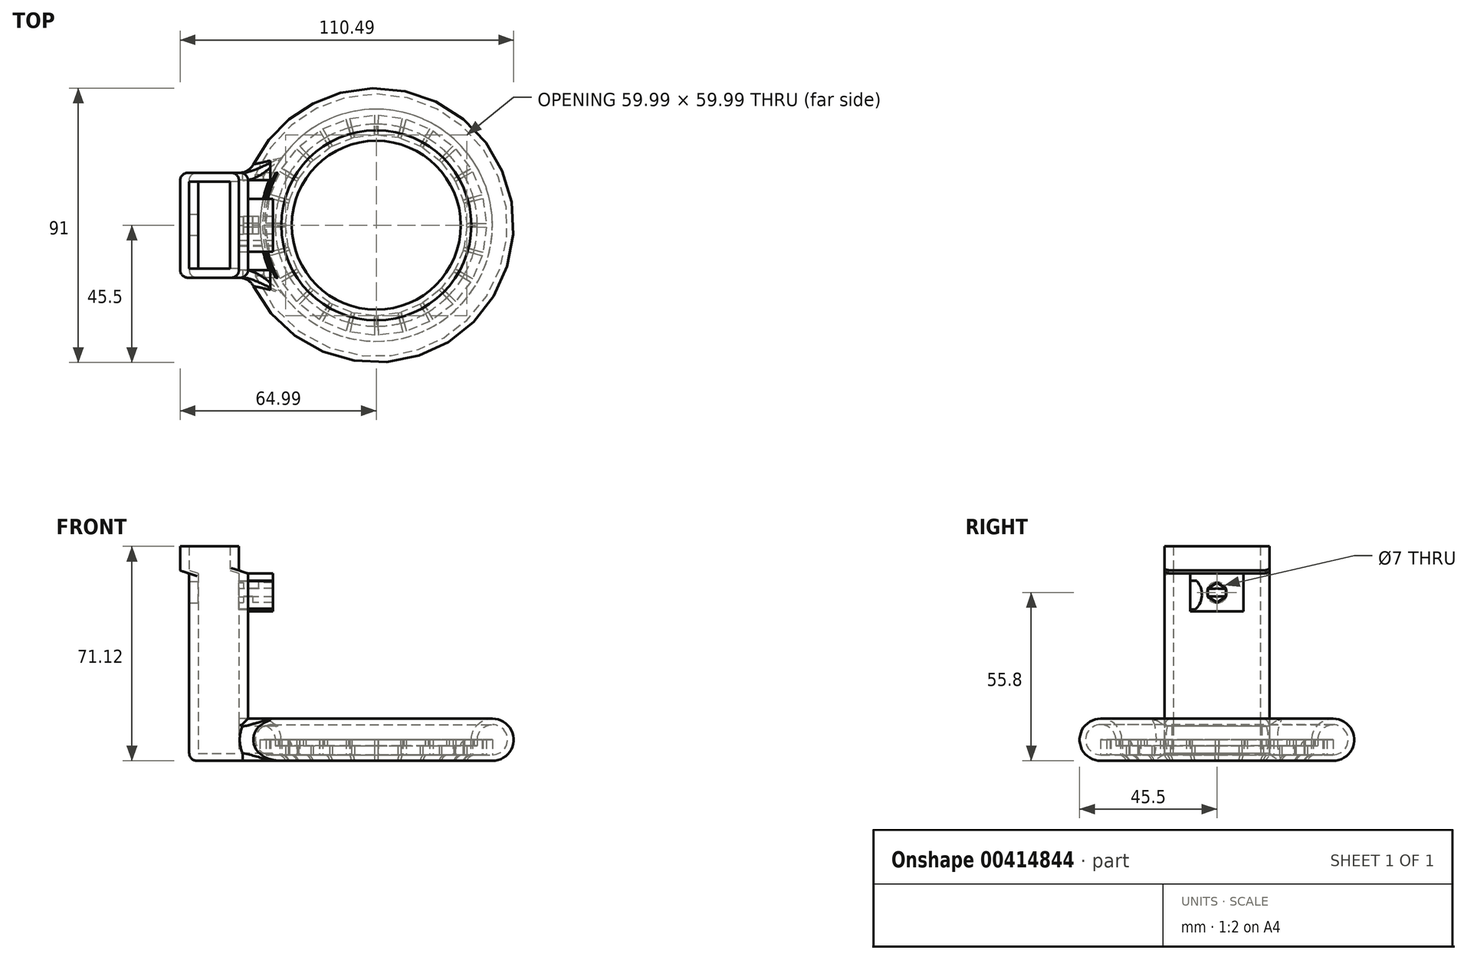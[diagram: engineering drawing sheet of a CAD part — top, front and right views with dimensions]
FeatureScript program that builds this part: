
annotation { "Feature Type Name" : "Feature", "Feature Type Description" : "" }
export const myFeature = defineFeature(function(context is Context, id is Id, definition is map)
    precondition{}
    {
        {
            var Q0;
            Q0=qCreatedBy(makeId("Right.planeOp"),FACE);
            cPlane(context, id + "F0", {"entities" : qUnion([Q0]), "cplaneType" : CPlaneType.OFFSET, "offset" : 42.5 * mm, "oppositeDirection" : true, "width" : 150 * mm, "height" : 150 * mm});
        }
        {
            var Q0;
            Q0=qCreatedBy(makeId("Front.planeOp"),FACE);
            cPlane(context, id + "F1", {"entities" : qUnion([Q0]), "cplaneType" : CPlaneType.OFFSET, "offset" : 17.41 * mm, "width" : 150 * mm, "height" : 150 * mm});
        }
        {
            var Q0;
            Q0=qCreatedBy(makeId("Front.planeOp"),FACE);
            cPlane(context, id + "F2", {"entities" : qUnion([Q0]), "cplaneType" : CPlaneType.OFFSET, "offset" : 17.41 * mm, "oppositeDirection" : true, "width" : 150 * mm, "height" : 150 * mm});
        }
        {
            var Q0;
            Q0=qCreatedBy(makeId("Top.planeOp"),FACE);
            cPlane(context, id + "F3", {"entities" : qUnion([Q0]), "cplaneType" : CPlaneType.OFFSET, "offset" : 7 * mm, "width" : 150 * mm, "height" : 150 * mm});
        }
        {
            var Q0;
            Q0=qCreatedBy(id+"F3.planeOp",FACE);
            cPlane(context, id + "F4", {"entities" : qUnion([Q0]), "cplaneType" : CPlaneType.OFFSET, "offset" : 6.95 * mm, "width" : 150 * mm, "height" : 150 * mm});
        }
        {
            var Q0;
            Q0=qCreatedBy(id+"F3.planeOp",FACE);
            cPlane(context, id + "F5", {"entities" : qUnion([Q0]), "cplaneType" : CPlaneType.OFFSET, "offset" : 55.12 * mm, "width" : 150 * mm, "height" : 150 * mm});
        }
        {
            var Q0;
            Q0=qCreatedBy(makeId("Right.planeOp"),FACE);
            cPlane(context, id + "F6", {"entities" : qUnion([Q0]), "cplaneType" : CPlaneType.OFFSET, "offset" : 62 * mm, "oppositeDirection" : true, "width" : 150 * mm, "height" : 150 * mm});
        }
        {
            var Q0;
            Q0=qCreatedBy(id+"F5.planeOp",FACE);
            cPlane(context, id + "F7", {"entities" : qUnion([Q0]), "cplaneType" : CPlaneType.OFFSET, "offset" : 1 * mm, "width" : 150 * mm, "height" : 150 * mm});
        }
        {
            var Q0;
            Q0=qCreatedBy(makeId("Top.planeOp"),FACE);
            var sketch = newSketch(context, id + "F8", { "sketchPlane" : qUnion([Q0])});
            skCircle(sketch, "E0", {"center": v(0, 0) * mm, "radius": 45 * mm});
            skCircle(sketch, "E1.0", {"center": v(0, 0) * mm, "radius": 38.5 * mm});
            skLineSegment(sketch, "E2", {"start": v(-136.41, 41.5) * mm, "end": v(-136.41, 35) * mm});
            skLineSegment(sketch, "E3", {"start": v(-128.72, 34) * mm, "end": v(-127.05, 40.28) * mm});
            skLineSegment(sketch, "E4", {"start": v(-118.16, 36.6) * mm, "end": v(-121.4, 30.99) * mm});
            skLineSegment(sketch, "E5", {"start": v(-115.15, 26.17) * mm, "end": v(-110.55, 30.76) * mm});
            skLineSegment(sketch, "E6", {"start": v(-110.44, 20.01) * mm, "end": v(-104.8, 23.26) * mm});
            skLineSegment(sketch, "E7", {"start": v(-107.45, 12.84) * mm, "end": v(-101.18, 14.54) * mm});
            skLineSegment(sketch, "E8", {"start": v(-106.41, 5.01) * mm, "end": v(-99.91, 5.01) * mm});
            skLineSegment(sketch, "E9.MirrorCS", {"start": v(-107.44, -2.81) * mm, "end": v(-101.17, -4.5) * mm});
            skLineSegment(sketch, "E10.MirrorCS", {"start": v(-110.42, -9.99) * mm, "end": v(-104.8, -13.24) * mm});
            skLineSegment(sketch, "E11.MirrorCS", {"start": v(-115.13, -16.15) * mm, "end": v(-110.52, -20.73) * mm});
            skLineSegment(sketch, "E12.MirrorCS", {"start": v(-118.13, -26.6) * mm, "end": v(-121.38, -20.97) * mm});
            skLineSegment(sketch, "E13.MirrorCS", {"start": v(-128.7, -24) * mm, "end": v(-127.02, -30.27) * mm});
            skLineSegment(sketch, "E14.MirrorCS", {"start": v(-144.1, 34) * mm, "end": v(-145.77, 40.28) * mm});
            skLineSegment(sketch, "E15.MirrorCS", {"start": v(-154.66, 36.6) * mm, "end": v(-151.41, 30.99) * mm});
            skLineSegment(sketch, "E16.MirrorCS", {"start": v(-157.67, 26.17) * mm, "end": v(-162.27, 30.76) * mm});
            skLineSegment(sketch, "E17.MirrorCS", {"start": v(-162.38, 20.01) * mm, "end": v(-168.01, 23.26) * mm});
            skLineSegment(sketch, "E18.MirrorCS", {"start": v(-165.37, 12.84) * mm, "end": v(-171.64, 14.54) * mm});
            skLineSegment(sketch, "E19.MirrorCS", {"start": v(-165.38, -2.81) * mm, "end": v(-171.65, -4.5) * mm});
            skLineSegment(sketch, "E20.MirrorCS", {"start": v(-162.4, -9.99) * mm, "end": v(-168.03, -13.24) * mm});
            skLineSegment(sketch, "E21.MirrorCS", {"start": v(-157.69, -16.15) * mm, "end": v(-162.3, -20.73) * mm});
            skLineSegment(sketch, "E22.MirrorCS", {"start": v(-154.69, -26.6) * mm, "end": v(-151.44, -20.97) * mm});
            skLineSegment(sketch, "E23.MirrorCS", {"start": v(-144.13, -24) * mm, "end": v(-145.8, -30.27) * mm});
            skLineSegment(sketch, "E24", {"start": v(-136.41, -25) * mm, "end": v(-136.41, -31.5) * mm});
            skLineSegment(sketch, "E25", {"start": v(-166.41, 5) * mm, "end": v(-172.91, 5) * mm});
            skCircle(sketch, "E26", {"center": v(-136.41, 5) * mm, "radius": 1.25 * mm, "construction": true});
            skLineSegment(sketch, "E27", {"start": v(0.64, 36.5) * mm, "end": v(0.52, 30) * mm});
            skLineSegment(sketch, "E28", {"start": v(8.2, 28.86) * mm, "end": v(9.97, 35.11) * mm});
            skLineSegment(sketch, "E29", {"start": v(18.8, 31.29) * mm, "end": v(15.46, 25.72) * mm});
            skLineSegment(sketch, "E30", {"start": v(21.62, 20.8) * mm, "end": v(26.3, 25.3) * mm});
            skLineSegment(sketch, "E31", {"start": v(26.23, 14.56) * mm, "end": v(31.92, 17.71) * mm});
            skLineSegment(sketch, "E32", {"start": v(29.1, 7.33) * mm, "end": v(35.4, 8.92) * mm});
            skLineSegment(sketch, "E33", {"start": v(30, -0.5) * mm, "end": v(36.5, -0.62) * mm});
            skLineSegment(sketch, "E34.MirrorCS", {"start": v(28.82, -8.32) * mm, "end": v(35.07, -10.12) * mm});
            skLineSegment(sketch, "E35.MirrorCS", {"start": v(25.72, -15.44) * mm, "end": v(31.3, -18.78) * mm});
            skLineSegment(sketch, "E36.MirrorCS", {"start": v(20.9, -21.52) * mm, "end": v(25.43, -26.18) * mm});
            skLineSegment(sketch, "E37.MirrorCS", {"start": v(17.73, -31.9) * mm, "end": v(14.57, -26.23) * mm});
            skLineSegment(sketch, "E38.MirrorCS", {"start": v(7.21, -29.12) * mm, "end": v(8.77, -35.43) * mm});
            skLineSegment(sketch, "E39.MirrorCS", {"start": v(-7.18, 29.13) * mm, "end": v(-8.74, 35.44) * mm});
            skLineSegment(sketch, "E40.MirrorCS", {"start": v(-17.7, 31.92) * mm, "end": v(-14.55, 26.25) * mm});
            skLineSegment(sketch, "E41.MirrorCS", {"start": v(-20.88, 21.54) * mm, "end": v(-25.4, 26.2) * mm});
            skLineSegment(sketch, "E42.MirrorCS", {"start": v(-25.7, 15.46) * mm, "end": v(-31.28, 18.81) * mm});
            skLineSegment(sketch, "E43.MirrorCS", {"start": v(-28.82, 8.34) * mm, "end": v(-35.06, 10.15) * mm});
            skLineSegment(sketch, "E44.MirrorCS", {"start": v(-29.1, -7.3) * mm, "end": v(-35.4, -8.89) * mm});
            skLineSegment(sketch, "E45.MirrorCS", {"start": v(-26.25, -14.53) * mm, "end": v(-31.93, -17.68) * mm});
            skLineSegment(sketch, "E46.MirrorCS", {"start": v(-21.64, -20.77) * mm, "end": v(-26.33, -25.28) * mm});
            skLineSegment(sketch, "E47.MirrorCS", {"start": v(-18.83, -31.27) * mm, "end": v(-15.48, -25.7) * mm});
            skLineSegment(sketch, "E48.MirrorCS", {"start": v(-8.22, -28.85) * mm, "end": v(-10, -35.1) * mm});
            skLineSegment(sketch, "E49", {"start": v(-0.52, -30) * mm, "end": v(-0.64, -36.5) * mm});
            skLineSegment(sketch, "E50", {"start": v(-30, 0.52) * mm, "end": v(-36.5, 0.64) * mm});
            skLineSegment(sketch, "E51", {"start": v(-0.64, 36.5) * mm, "end": v(-0.52, 30) * mm});
            skLineSegment(sketch, "E52", {"start": v(7.18, 29.13) * mm, "end": v(8.74, 35.44) * mm});
            skLineSegment(sketch, "E53", {"start": v(17.7, 31.92) * mm, "end": v(14.55, 26.25) * mm});
            skLineSegment(sketch, "E54", {"start": v(20.88, 21.54) * mm, "end": v(25.4, 26.2) * mm});
            skLineSegment(sketch, "E55", {"start": v(25.7, 15.46) * mm, "end": v(31.28, 18.81) * mm});
            skLineSegment(sketch, "E56", {"start": v(28.82, 8.34) * mm, "end": v(35.06, 10.15) * mm});
            skLineSegment(sketch, "E57", {"start": v(30, 0.54) * mm, "end": v(36.5, 0.65) * mm});
            skLineSegment(sketch, "E58.MirrorCS", {"start": v(29.1, -7.3) * mm, "end": v(35.4, -8.89) * mm});
            skLineSegment(sketch, "E59.MirrorCS", {"start": v(26.25, -14.53) * mm, "end": v(31.93, -17.68) * mm});
            skLineSegment(sketch, "E60.MirrorCS", {"start": v(21.64, -20.77) * mm, "end": v(26.33, -25.28) * mm});
            skLineSegment(sketch, "E61.MirrorCS", {"start": v(18.83, -31.27) * mm, "end": v(15.48, -25.7) * mm});
            skLineSegment(sketch, "E62.MirrorCS", {"start": v(8.22, -28.85) * mm, "end": v(10, -35.1) * mm});
            skLineSegment(sketch, "E63.MirrorCS", {"start": v(-8.2, 28.86) * mm, "end": v(-9.97, 35.11) * mm});
            skLineSegment(sketch, "E64.MirrorCS", {"start": v(-18.8, 31.29) * mm, "end": v(-15.46, 25.72) * mm});
            skLineSegment(sketch, "E65.MirrorCS", {"start": v(-21.62, 20.8) * mm, "end": v(-26.3, 25.3) * mm});
            skLineSegment(sketch, "E66.MirrorCS", {"start": v(-26.23, 14.56) * mm, "end": v(-31.92, 17.71) * mm});
            skLineSegment(sketch, "E67.MirrorCS", {"start": v(-29.1, 7.33) * mm, "end": v(-35.4, 8.92) * mm});
            skLineSegment(sketch, "E68.MirrorCS", {"start": v(-28.82, -8.32) * mm, "end": v(-35.07, -10.12) * mm});
            skLineSegment(sketch, "E69.MirrorCS", {"start": v(-25.72, -15.44) * mm, "end": v(-31.3, -18.78) * mm});
            skLineSegment(sketch, "E70.MirrorCS", {"start": v(-20.9, -21.52) * mm, "end": v(-25.43, -26.18) * mm});
            skLineSegment(sketch, "E71.MirrorCS", {"start": v(-17.73, -31.9) * mm, "end": v(-14.57, -26.23) * mm});
            skLineSegment(sketch, "E72.MirrorCS", {"start": v(-7.21, -29.12) * mm, "end": v(-8.77, -35.43) * mm});
            skLineSegment(sketch, "E73", {"start": v(0.52, -30) * mm, "end": v(0.64, -36.5) * mm});
            skLineSegment(sketch, "E74", {"start": v(-30, -0.52) * mm, "end": v(-36.5, -0.64) * mm});
            skCircle(sketch, "E75", {"center": v(0, 0) * mm, "radius": 1.25 * mm, "construction": true});
            skLineSegment(sketch, "E76", {"start": v(-29.1, 7.33) * mm, "end": v(-28.82, 8.34) * mm});
            skLineSegment(sketch, "E77", {"start": v(-28.82, 8.34) * mm, "end": v(-26.23, 14.56) * mm});
            skLineSegment(sketch, "E78", {"start": v(-26.23, 14.56) * mm, "end": v(-25.7, 15.46) * mm});
            skLineSegment(sketch, "E79", {"start": v(-25.7, 15.46) * mm, "end": v(-21.62, 20.8) * mm});
            skLineSegment(sketch, "E80", {"start": v(-21.62, 20.8) * mm, "end": v(-20.88, 21.54) * mm});
            skLineSegment(sketch, "E81", {"start": v(-20.88, 21.54) * mm, "end": v(-15.46, 25.72) * mm});
            skLineSegment(sketch, "E82", {"start": v(-15.46, 25.72) * mm, "end": v(-14.55, 26.25) * mm});
            skLineSegment(sketch, "E83", {"start": v(-14.55, 26.25) * mm, "end": v(-8.2, 28.86) * mm});
            skLineSegment(sketch, "E84", {"start": v(-8.2, 28.86) * mm, "end": v(-7.18, 29.13) * mm});
            skLineSegment(sketch, "E85", {"start": v(-7.18, 29.13) * mm, "end": v(-0.52, 30) * mm});
            skLineSegment(sketch, "E86", {"start": v(-0.52, 30) * mm, "end": v(0.52, 30) * mm});
            skLineSegment(sketch, "E87", {"start": v(0.52, 30) * mm, "end": v(7.18, 29.13) * mm});
            skLineSegment(sketch, "E88", {"start": v(7.18, 29.13) * mm, "end": v(8.2, 28.86) * mm});
            skLineSegment(sketch, "E89", {"start": v(8.2, 28.86) * mm, "end": v(14.55, 26.25) * mm});
            skLineSegment(sketch, "E90", {"start": v(14.55, 26.25) * mm, "end": v(15.46, 25.72) * mm});
            skLineSegment(sketch, "E91", {"start": v(15.46, 25.72) * mm, "end": v(20.88, 21.54) * mm});
            skLineSegment(sketch, "E92", {"start": v(20.88, 21.54) * mm, "end": v(21.62, 20.8) * mm});
            skLineSegment(sketch, "E93", {"start": v(21.62, 20.8) * mm, "end": v(25.7, 15.46) * mm});
            skLineSegment(sketch, "E94", {"start": v(25.7, 15.46) * mm, "end": v(26.23, 14.56) * mm});
            skLineSegment(sketch, "E95", {"start": v(26.23, 14.56) * mm, "end": v(28.82, 8.34) * mm});
            skLineSegment(sketch, "E96", {"start": v(28.82, 8.34) * mm, "end": v(29.1, 7.33) * mm});
            skLineSegment(sketch, "E97", {"start": v(29.1, 7.33) * mm, "end": v(30, 0.54) * mm});
            skLineSegment(sketch, "E98", {"start": v(30, 0.54) * mm, "end": v(30, -0.5) * mm});
            skLineSegment(sketch, "E99", {"start": v(30, -0.5) * mm, "end": v(29.1, -7.3) * mm});
            skLineSegment(sketch, "E100", {"start": v(29.1, -7.3) * mm, "end": v(28.82, -8.32) * mm});
            skLineSegment(sketch, "E101", {"start": v(28.82, -8.32) * mm, "end": v(26.25, -14.53) * mm});
            skLineSegment(sketch, "E102", {"start": v(26.25, -14.53) * mm, "end": v(25.72, -15.44) * mm});
            skLineSegment(sketch, "E103", {"start": v(25.72, -15.44) * mm, "end": v(21.64, -20.77) * mm});
            skLineSegment(sketch, "E104", {"start": v(21.64, -20.77) * mm, "end": v(20.9, -21.52) * mm});
            skLineSegment(sketch, "E105", {"start": v(20.9, -21.52) * mm, "end": v(15.48, -25.7) * mm});
            skLineSegment(sketch, "E106", {"start": v(15.48, -25.7) * mm, "end": v(14.57, -26.23) * mm});
            skLineSegment(sketch, "E107", {"start": v(14.57, -26.23) * mm, "end": v(8.22, -28.85) * mm});
            skLineSegment(sketch, "E108", {"start": v(8.22, -28.85) * mm, "end": v(7.21, -29.12) * mm});
            skLineSegment(sketch, "E109", {"start": v(7.21, -29.12) * mm, "end": v(0.52, -30) * mm});
            skLineSegment(sketch, "E110", {"start": v(0.52, -30) * mm, "end": v(-0.52, -30) * mm});
            skLineSegment(sketch, "E111", {"start": v(-0.52, -30) * mm, "end": v(-7.21, -29.12) * mm});
            skLineSegment(sketch, "E112", {"start": v(-7.21, -29.12) * mm, "end": v(-8.22, -28.85) * mm});
            skLineSegment(sketch, "E113", {"start": v(-8.22, -28.85) * mm, "end": v(-14.57, -26.23) * mm});
            skLineSegment(sketch, "E114", {"start": v(-14.57, -26.23) * mm, "end": v(-15.48, -25.7) * mm});
            skLineSegment(sketch, "E115", {"start": v(-15.48, -25.7) * mm, "end": v(-20.9, -21.52) * mm});
            skLineSegment(sketch, "E116", {"start": v(-20.9, -21.52) * mm, "end": v(-21.64, -20.77) * mm});
            skLineSegment(sketch, "E117", {"start": v(-21.64, -20.77) * mm, "end": v(-25.72, -15.44) * mm});
            skLineSegment(sketch, "E118", {"start": v(-25.72, -15.44) * mm, "end": v(-26.25, -14.53) * mm});
            skLineSegment(sketch, "E119", {"start": v(-28.82, -8.32) * mm, "end": v(-29.1, -7.3) * mm});
            skLineSegment(sketch, "E120", {"start": v(-26.25, -14.53) * mm, "end": v(-28.82, -8.32) * mm});
            skLineSegment(sketch, "E121", {"start": v(-29.1, -7.3) * mm, "end": v(-30, -0.52) * mm});
            skLineSegment(sketch, "E122", {"start": v(-30, -0.52) * mm, "end": v(-30, 0.52) * mm});
            skLineSegment(sketch, "E123", {"start": v(-30, 0.52) * mm, "end": v(-29.1, 7.33) * mm});
            skLineSegment(sketch, "E124", {"start": v(-36.5, 0.64) * mm, "end": v(-35.4, 8.92) * mm});
            skLineSegment(sketch, "E125", {"start": v(-35.06, 10.15) * mm, "end": v(-31.92, 17.71) * mm});
            skLineSegment(sketch, "E126", {"start": v(-31.28, 18.81) * mm, "end": v(-26.3, 25.3) * mm});
            skLineSegment(sketch, "E127", {"start": v(-25.4, 26.2) * mm, "end": v(-18.8, 31.29) * mm});
            skLineSegment(sketch, "E128", {"start": v(-17.7, 31.92) * mm, "end": v(-9.97, 35.11) * mm});
            skLineSegment(sketch, "E129", {"start": v(-8.74, 35.44) * mm, "end": v(-0.64, 36.5) * mm});
            skLineSegment(sketch, "E130", {"start": v(0.64, 36.5) * mm, "end": v(8.74, 35.44) * mm});
            skLineSegment(sketch, "E131", {"start": v(9.97, 35.11) * mm, "end": v(17.7, 31.92) * mm});
            skLineSegment(sketch, "E132", {"start": v(18.8, 31.29) * mm, "end": v(25.4, 26.2) * mm});
            skLineSegment(sketch, "E133", {"start": v(26.3, 25.3) * mm, "end": v(31.28, 18.81) * mm});
            skLineSegment(sketch, "E134", {"start": v(31.92, 17.71) * mm, "end": v(35.06, 10.15) * mm});
            skLineSegment(sketch, "E135", {"start": v(35.4, 8.92) * mm, "end": v(36.5, 0.65) * mm});
            skLineSegment(sketch, "E136", {"start": v(36.5, -0.62) * mm, "end": v(35.4, -8.89) * mm});
            skLineSegment(sketch, "E137", {"start": v(35.07, -10.12) * mm, "end": v(31.93, -17.68) * mm});
            skLineSegment(sketch, "E138", {"start": v(31.3, -18.78) * mm, "end": v(26.33, -25.28) * mm});
            skLineSegment(sketch, "E139", {"start": v(25.43, -26.18) * mm, "end": v(18.83, -31.27) * mm});
            skLineSegment(sketch, "E140", {"start": v(17.73, -31.9) * mm, "end": v(10, -35.1) * mm});
            skLineSegment(sketch, "E141", {"start": v(8.77, -35.43) * mm, "end": v(0.64, -36.5) * mm});
            skLineSegment(sketch, "E142", {"start": v(-0.64, -36.5) * mm, "end": v(-8.77, -35.43) * mm});
            skLineSegment(sketch, "E143", {"start": v(-10, -35.1) * mm, "end": v(-17.73, -31.9) * mm});
            skLineSegment(sketch, "E144", {"start": v(-18.83, -31.27) * mm, "end": v(-25.43, -26.18) * mm});
            skLineSegment(sketch, "E145", {"start": v(-26.33, -25.28) * mm, "end": v(-31.3, -18.78) * mm});
            skLineSegment(sketch, "E146", {"start": v(-31.93, -17.68) * mm, "end": v(-35.07, -10.12) * mm});
            skLineSegment(sketch, "E147", {"start": v(-35.4, -8.89) * mm, "end": v(-36.5, -0.64) * mm});
            skSolve(sketch);
        }
        {
            var Q0;
            Q0=qCreatedBy(makeId("Front.planeOp"),FACE);
            var sketch = newSketch(context, id + "F9", { "sketchPlane" : qUnion([Q0])});
            skLineSegment(sketch, "E148.bottom", {"start": v(38.5, 7) * mm, "end": v(-38.5, 7) * mm, "construction": true});
            skLineSegment(sketch, "E148.top", {"start": v(38.5, -7) * mm, "end": v(-38.5, -7) * mm, "construction": true});
            skLineSegment(sketch, "E148.left", {"start": v(38.5, 7) * mm, "end": v(38.5, -7) * mm, "construction": true});
            skLineSegment(sketch, "E148.right", {"start": v(-38.5, 7) * mm, "end": v(-38.5, -7) * mm, "construction": true});
            skPoint(sketch, "E148.middle", {"position": v(0, 0) * mm});
            skLineSegment(sketch, "E149", {"start": v(-38.5, 0) * mm, "end": v(38.5, 0) * mm, "construction": true});
            skArc(sketch, "E150", {"start": v(38.5, 0) * mm, "mid": v(43.45, 11.95) * mm, "end": v(31.5, 7) * mm});
            skArc(sketch, "E151", {"start": v(38.5, 2) * mm, "mid": v(42.04, 10.54) * mm, "end": v(33.5, 7) * mm});
            skLineSegment(sketch, "E152", {"start": v(38.5, 2) * mm, "end": v(38.5, 0) * mm});
            skLineSegment(sketch, "E153", {"start": v(38.5, 2) * mm, "end": v(31.5, 2) * mm, "construction": true});
            skLineSegment(sketch, "E154", {"start": v(31.5, 2) * mm, "end": v(31.5, 0) * mm, "construction": true});
            skLineSegment(sketch, "E155.0", {"start": v(38.5, 5) * mm, "end": v(-38.5, 5) * mm, "construction": true});
            skLineSegment(sketch, "E156", {"start": v(30, 0) * mm, "end": v(30, 7) * mm, "construction": true});
            skLineSegment(sketch, "E157", {"start": v(31.5, 7) * mm, "end": v(30, 7) * mm});
            skLineSegment(sketch, "E158", {"start": v(30, 7) * mm, "end": v(30, 5) * mm});
            skLineSegment(sketch, "E159", {"start": v(30, 5) * mm, "end": v(33.5, 5) * mm});
            skLineSegment(sketch, "E160", {"start": v(33.5, 5) * mm, "end": v(33.5, 7) * mm});
            skLineSegment(sketch, "E161", {"start": v(0, -7) * mm, "end": v(0, 7) * mm, "construction": true});
            skLineSegment(sketch, "E162", {"start": v(38.5, 7) * mm, "end": v(38.5, 14) * mm, "construction": true});
            skLineSegment(sketch, "E163", {"start": v(38.5, 7) * mm, "end": v(45.5, 7) * mm, "construction": true});
            skLineSegment(sketch, "E164", {"start": v(38.5, 12) * mm, "end": v(38.5, 14) * mm});
            skLineSegment(sketch, "E165", {"start": v(43.5, 7) * mm, "end": v(45.5, 7) * mm});
            skLineSegment(sketch, "E166.MirrorCS", {"start": v(-38.5, 2) * mm, "end": v(-38.5, 0) * mm});
            skLineSegment(sketch, "E167.MirrorCS", {"start": v(-30, 7) * mm, "end": v(-30, 5) * mm});
            skLineSegment(sketch, "E168.MirrorCS", {"start": v(-31.5, 7) * mm, "end": v(-30, 7) * mm});
            skLineSegment(sketch, "E169.MirrorCS", {"start": v(-33.5, 5) * mm, "end": v(-33.5, 7) * mm});
            skLineSegment(sketch, "E170.MirrorCS", {"start": v(-43.5, 7) * mm, "end": v(-45.5, 7) * mm});
            skLineSegment(sketch, "E171.MirrorCS", {"start": v(-30, 5) * mm, "end": v(-33.5, 5) * mm});
            skLineSegment(sketch, "E172.MirrorCS", {"start": v(-31.5, 2) * mm, "end": v(-31.5, 0) * mm, "construction": true});
            skLineSegment(sketch, "E173.MirrorCS", {"start": v(-38.5, 12) * mm, "end": v(-38.5, 14) * mm});
            skLineSegment(sketch, "E174.MirrorCS", {"start": v(-38.5, 7) * mm, "end": v(-45.5, 7) * mm, "construction": true});
            skLineSegment(sketch, "E175.MirrorCS", {"start": v(-38.5, 2) * mm, "end": v(-31.5, 2) * mm, "construction": true});
            skLineSegment(sketch, "E176.MirrorCS", {"start": v(-38.5, 7) * mm, "end": v(-38.5, 14) * mm, "construction": true});
            skArc(sketch, "E177.MirrorCS", {"start": v(-38.5, 0) * mm, "mid": v(-43.45, 11.95) * mm, "end": v(-31.5, 7) * mm});
            skArc(sketch, "E178.MirrorCS", {"start": v(-38.5, 2) * mm, "mid": v(-42.04, 10.54) * mm, "end": v(-33.5, 7) * mm});
            skLineSegment(sketch, "E179.MirrorCS", {"start": v(-38.5, 5) * mm, "end": v(38.5, 5) * mm, "construction": true});
            skLineSegment(sketch, "E180.MirrorCS", {"start": v(-30, 0) * mm, "end": v(-30, 7) * mm, "construction": true});
            skLineSegment(sketch, "E181.MirrorCS", {"start": v(-38.5, 7) * mm, "end": v(38.5, 7) * mm, "construction": true});
            skArc(sketch, "E182", {"start": v(30, 7) * mm, "mid": v(28.58, 6.41) * mm, "end": v(28, 5) * mm});
            skLineSegment(sketch, "E183", {"start": v(28, 5) * mm, "end": v(30, 5) * mm});
            skArc(sketch, "E184.MirrorCS", {"start": v(-30, 7) * mm, "mid": v(-28.58, 6.41) * mm, "end": v(-28, 5) * mm});
            skLineSegment(sketch, "E185", {"start": v(-30, 5) * mm, "end": v(-28, 5) * mm});
            skSolve(sketch);
        }
        {
            var Q0;
            Q0=qCreatedBy(id+"F0.planeOp",FACE);
            var sketch = newSketch(context, id + "F10", { "sketchPlane" : qUnion([Q0])});
            skLineSegment(sketch, "E186.bottom", {"start": v(45.5, 14) * mm, "end": v(-45.5, 14) * mm, "construction": true});
            skLineSegment(sketch, "E186.top", {"start": v(45.5, -14) * mm, "end": v(-45.5, -14) * mm, "construction": true});
            skLineSegment(sketch, "E186.left", {"start": v(45.5, 14) * mm, "end": v(45.5, -14) * mm, "construction": true});
            skLineSegment(sketch, "E186.right", {"start": v(-45.5, 14) * mm, "end": v(-45.5, -14) * mm, "construction": true});
            skPoint(sketch, "E186.middle", {"position": v(0, 0) * mm});
            skLineSegment(sketch, "E187", {"start": v(-45.5, 0) * mm, "end": v(45.5, 0) * mm, "construction": true});
            skLineSegment(sketch, "E188", {"start": v(0, 14) * mm, "end": v(0, -14) * mm, "construction": true});
            skLineSegment(sketch, "E189.0", {"start": v(-17.41, 14) * mm, "end": v(-17.41, -14) * mm, "construction": true});
            skLineSegment(sketch, "E190.MirrorCS", {"start": v(17.41, 14) * mm, "end": v(17.41, -14) * mm, "construction": true});
            skLineSegment(sketch, "E191.0", {"start": v(45.5, 7) * mm, "end": v(-45.5, 7) * mm, "construction": true});
            skLineSegment(sketch, "E192", {"start": v(-17.41, 14) * mm, "end": v(-17.41, 7) * mm});
            skLineSegment(sketch, "E193", {"start": v(-17.41, 7) * mm, "end": v(17.41, 7) * mm});
            skLineSegment(sketch, "E194", {"start": v(17.41, 7) * mm, "end": v(17.41, 14) * mm});
            skLineSegment(sketch, "E195", {"start": v(17.41, 14) * mm, "end": v(-17.41, 14) * mm});
            skLineSegment(sketch, "E196.0", {"start": v(45.5, 12) * mm, "end": v(-45.5, 12) * mm, "construction": true});
            skLineSegment(sketch, "E197.0", {"start": v(-14.73, 14) * mm, "end": v(-14.73, -14) * mm, "construction": true});
            skLineSegment(sketch, "E198.MirrorCS", {"start": v(14.73, 14) * mm, "end": v(14.73, -14) * mm, "construction": true});
            skLineSegment(sketch, "E199", {"start": v(-14.73, 7) * mm, "end": v(-14.73, 14) * mm});
            skLineSegment(sketch, "E200", {"start": v(14.73, 7) * mm, "end": v(14.73, 14) * mm});
            skLineSegment(sketch, "E201", {"start": v(17.41, 12) * mm, "end": v(-17.41, 12) * mm});
            skPoint(sketch, "E201.startSnap0", {"position": v(17.41, 10.5) * mm});
            skArc(sketch, "E202.0", {"start": v(6.63, 59.56) * mm, "mid": v(4.95, 54.97) * mm, "end": v(6.87, 50.47) * mm});
            skArc(sketch, "E203.MirrorCS", {"start": v(-6.63, 59.56) * mm, "mid": v(-4.95, 54.97) * mm, "end": v(-6.87, 50.47) * mm});
            skLineSegment(sketch, "E204", {"start": v(-6.63, 59.72) * mm, "end": v(6.63, 59.72) * mm});
            skLineSegment(sketch, "E205.1", {"start": v(-2.98, 51.95) * mm, "end": v(2.98, 51.95) * mm});
            skLineSegment(sketch, "E206", {"start": v(-8.8, 49.55) * mm, "end": v(-8.8, 62.12) * mm});
            skLineSegment(sketch, "E207.MirrorCS", {"start": v(8.8, 49.55) * mm, "end": v(8.8, 62.12) * mm});
            skLineSegment(sketch, "E208", {"start": v(-8.8, 62.12) * mm, "end": v(8.8, 62.12) * mm});
            skLineSegment(sketch, "E209", {"start": v(-6.63, 59.72) * mm, "end": v(-8.8, 59.72) * mm});
            skLineSegment(sketch, "E210", {"start": v(6.63, 59.72) * mm, "end": v(8.8, 59.72) * mm});
            skLineSegment(sketch, "E211", {"start": v(-2.98, 51.95) * mm, "end": v(-6.87, 50.26) * mm});
            skLineSegment(sketch, "E212", {"start": v(-6.87, 50.47) * mm, "end": v(-6.87, 50.26) * mm});
            skLineSegment(sketch, "E213.MirrorCS", {"start": v(2.98, 51.95) * mm, "end": v(6.87, 50.26) * mm});
            skLineSegment(sketch, "E214.MirrorCS", {"start": v(6.87, 50.47) * mm, "end": v(6.87, 50.26) * mm});
            skLineSegment(sketch, "E215", {"start": v(-8.8, 49.55) * mm, "end": v(8.8, 49.55) * mm});
            skLineSegment(sketch, "E216", {"start": v(6.87, 50.26) * mm, "end": v(8.8, 50.26) * mm});
            skLineSegment(sketch, "E217", {"start": v(-6.87, 50.26) * mm, "end": v(-8.8, 50.26) * mm});
            skCircle(sketch, "E218", {"center": v(0, 0) * mm, "radius": 1.5 * mm, "construction": true});
            skCircle(sketch, "E219", {"center": v(0, 55.8) * mm, "radius": 1.39 * mm});
            skLineSegment(sketch, "E220", {"start": v(6.63, 59.56) * mm, "end": v(6.63, 59.72) * mm});
            skLineSegment(sketch, "E221", {"start": v(-6.63, 59.56) * mm, "end": v(-6.63, 59.72) * mm});
            skLineSegment(sketch, "E222.1", {"start": v(0, 52.5) * mm, "end": v(2.95, 54.35) * mm});
            skLineSegment(sketch, "E222.2", {"start": v(-2.95, 54.35) * mm, "end": v(0, 52.5) * mm});
            skLineSegment(sketch, "E223.MirrorCS", {"start": v(0, 59.1) * mm, "end": v(2.95, 57.25) * mm});
            skLineSegment(sketch, "E224.MirrorCS", {"start": v(-2.95, 57.25) * mm, "end": v(0, 59.1) * mm});
            skLineSegment(sketch, "E225", {"start": v(2.95, 57.25) * mm, "end": v(2.95, 54.35) * mm});
            skLineSegment(sketch, "E226", {"start": v(-2.95, 57.25) * mm, "end": v(-2.95, 54.35) * mm});
            skCircle(sketch, "E227", {"center": v(0, 55.8) * mm, "radius": 1.25 * mm, "construction": true});
            skLineSegment(sketch, "E228", {"start": v(-2.95, 54.55) * mm, "end": v(2.95, 54.55) * mm});
            skLineSegment(sketch, "E229", {"start": v(-2.95, 57.05) * mm, "end": v(2.95, 57.05) * mm});
            skLineSegment(sketch, "E230", {"start": v(14.73, 14) * mm, "end": v(14.73, 52.5) * mm});
            skLineSegment(sketch, "E231", {"start": v(0, 55.8) * mm, "end": v(0, 14) * mm, "construction": true});
            skLineSegment(sketch, "E232.MirrorCS", {"start": v(-14.73, 14) * mm, "end": v(-14.73, 52.5) * mm});
            skLineSegment(sketch, "E233", {"start": v(17.41, 14) * mm, "end": v(17.41, 52.5) * mm});
            skLineSegment(sketch, "E234", {"start": v(-17.41, 14) * mm, "end": v(-17.41, 52.5) * mm});
            skLineSegment(sketch, "E235", {"start": v(-8.8, 62.12) * mm, "end": v(-17.41, 62.12) * mm});
            skLineSegment(sketch, "E236", {"start": v(8.8, 62.12) * mm, "end": v(17.41, 62.12) * mm});
            skLineSegment(sketch, "E237", {"start": v(17.41, 52.5) * mm, "end": v(17.41, 62.12) * mm});
            skLineSegment(sketch, "E238", {"start": v(14.73, 52.5) * mm, "end": v(14.73, 62.12) * mm});
            skLineSegment(sketch, "E239", {"start": v(-14.73, 52.5) * mm, "end": v(-14.73, 62.12) * mm});
            skLineSegment(sketch, "E240", {"start": v(-17.41, 52.5) * mm, "end": v(-17.41, 62.12) * mm});
            skSolve(sketch);
        }
        {
            var Q0;
            Q0=qCreatedBy(id+"F1.planeOp",FACE);
            var sketch = newSketch(context, id + "F11", { "sketchPlane" : qUnion([Q0])});
            skLineSegment(sketch, "E241.bottom", {"start": v(45.5, 14) * mm, "end": v(-45.5, 14) * mm, "construction": true});
            skLineSegment(sketch, "E241.top", {"start": v(45.5, -14) * mm, "end": v(-45.5, -14) * mm, "construction": true});
            skLineSegment(sketch, "E241.left", {"start": v(45.5, 14) * mm, "end": v(45.5, -14) * mm, "construction": true});
            skLineSegment(sketch, "E241.right", {"start": v(-45.5, 14) * mm, "end": v(-45.5, -14) * mm, "construction": true});
            skPoint(sketch, "E241.middle", {"position": v(0, 0) * mm});
            skLineSegment(sketch, "E242", {"start": v(-45.5, 0) * mm, "end": v(45.5, 0) * mm, "construction": true});
            skLineSegment(sketch, "E243", {"start": v(0, 14) * mm, "end": v(0, -14) * mm, "construction": true});
            skLineSegment(sketch, "E244.0", {"start": v(-17.41, 14) * mm, "end": v(-17.41, -14) * mm, "construction": true});
            skLineSegment(sketch, "E245.MirrorCS", {"start": v(17.41, 14) * mm, "end": v(17.41, -14) * mm, "construction": true});
            skLineSegment(sketch, "E246.0", {"start": v(45.5, 7) * mm, "end": v(-45.5, 7) * mm, "construction": true});
            skLineSegment(sketch, "E247", {"start": v(-17.41, 14) * mm, "end": v(-17.41, 7) * mm});
            skLineSegment(sketch, "E248", {"start": v(-17.41, 7) * mm, "end": v(17.41, 7) * mm});
            skLineSegment(sketch, "E249", {"start": v(17.41, 7) * mm, "end": v(17.41, 14) * mm});
            skLineSegment(sketch, "E250", {"start": v(17.41, 14) * mm, "end": v(-17.41, 14) * mm});
            skLineSegment(sketch, "E251.0", {"start": v(45.5, 12) * mm, "end": v(-45.5, 12) * mm, "construction": true});
            skLineSegment(sketch, "E252.0", {"start": v(-14.73, 14) * mm, "end": v(-14.73, -14) * mm, "construction": true});
            skLineSegment(sketch, "E253.MirrorCS", {"start": v(14.73, 14) * mm, "end": v(14.73, -14) * mm, "construction": true});
            skLineSegment(sketch, "E254", {"start": v(-14.73, 7) * mm, "end": v(-14.73, 14) * mm});
            skLineSegment(sketch, "E255", {"start": v(14.73, 7) * mm, "end": v(14.73, 14) * mm});
            skLineSegment(sketch, "E256", {"start": v(17.41, 12) * mm, "end": v(-17.41, 12) * mm});
            skPoint(sketch, "E256.startSnap0", {"position": v(17.41, 10.5) * mm});
            skLineSegment(sketch, "E257", {"start": v(45.5, 14) * mm, "end": v(45.5, 7) * mm});
            skCircle(sketch, "E258", {"center": v(-35.07, 7) * mm, "radius": 7 * mm, "construction": true});
            skArc(sketch, "E259", {"start": v(-35.07, 12) * mm, "mid": v(-40.07, 7) * mm, "end": v(-35.07, 2) * mm});
            skLineSegment(sketch, "E260", {"start": v(-35.07, 12) * mm, "end": v(-35.07, 14) * mm});
            skLineSegment(sketch, "E261", {"start": v(-35.07, 14) * mm, "end": v(-45.5, 14) * mm});
            skLineSegment(sketch, "E262", {"start": v(-45.5, 14) * mm, "end": v(-45.5, 0) * mm});
            skLineSegment(sketch, "E263", {"start": v(-45.5, 0) * mm, "end": v(-35.07, 0) * mm});
            skLineSegment(sketch, "E264", {"start": v(-35.07, 0) * mm, "end": v(-35.07, 2) * mm});
            skLineSegment(sketch, "E265.MirrorCS", {"start": v(45.5, 2) * mm, "end": v(-45.5, 2) * mm, "construction": true});
            skCircle(sketch, "E266", {"center": v(0, 7) * mm, "radius": 1.25 * mm, "construction": true});
            skSolve(sketch);
        }
        {
            var Q0;
            Q0=qCreatedBy(id+"F2.planeOp",FACE);
            var sketch = newSketch(context, id + "F12", { "sketchPlane" : qUnion([Q0])});
            skLineSegment(sketch, "E267.bottom", {"start": v(45.5, 14) * mm, "end": v(-45.5, 14) * mm, "construction": true});
            skLineSegment(sketch, "E267.top", {"start": v(45.5, -14) * mm, "end": v(-45.5, -14) * mm, "construction": true});
            skLineSegment(sketch, "E267.left", {"start": v(45.5, 14) * mm, "end": v(45.5, -14) * mm, "construction": true});
            skLineSegment(sketch, "E267.right", {"start": v(-45.5, 14) * mm, "end": v(-45.5, -14) * mm, "construction": true});
            skPoint(sketch, "E267.middle", {"position": v(0, 0) * mm});
            skLineSegment(sketch, "E268", {"start": v(-45.5, 0) * mm, "end": v(45.5, 0) * mm, "construction": true});
            skLineSegment(sketch, "E269", {"start": v(0, 14) * mm, "end": v(0, -14) * mm, "construction": true});
            skLineSegment(sketch, "E270.0", {"start": v(-17.41, 14) * mm, "end": v(-17.41, -14) * mm, "construction": true});
            skLineSegment(sketch, "E271.MirrorCS", {"start": v(17.41, 14) * mm, "end": v(17.41, -14) * mm, "construction": true});
            skLineSegment(sketch, "E272.0", {"start": v(45.5, 7) * mm, "end": v(-45.5, 7) * mm, "construction": true});
            skLineSegment(sketch, "E273", {"start": v(-17.41, 14) * mm, "end": v(-17.41, 7) * mm});
            skLineSegment(sketch, "E274", {"start": v(-17.41, 7) * mm, "end": v(17.41, 7) * mm});
            skLineSegment(sketch, "E275", {"start": v(17.41, 7) * mm, "end": v(17.41, 14) * mm});
            skLineSegment(sketch, "E276", {"start": v(17.41, 14) * mm, "end": v(-17.41, 14) * mm});
            skLineSegment(sketch, "E277.0", {"start": v(45.5, 12) * mm, "end": v(-45.5, 12) * mm, "construction": true});
            skLineSegment(sketch, "E278.0", {"start": v(-14.73, 14) * mm, "end": v(-14.73, -14) * mm, "construction": true});
            skLineSegment(sketch, "E279.MirrorCS", {"start": v(14.73, 14) * mm, "end": v(14.73, -14) * mm, "construction": true});
            skLineSegment(sketch, "E280", {"start": v(-14.73, 7) * mm, "end": v(-14.73, 14) * mm});
            skLineSegment(sketch, "E281", {"start": v(14.73, 7) * mm, "end": v(14.73, 14) * mm});
            skLineSegment(sketch, "E282", {"start": v(17.41, 12) * mm, "end": v(-17.41, 12) * mm});
            skPoint(sketch, "E282.startSnap0", {"position": v(17.41, 10.5) * mm});
            skLineSegment(sketch, "E283", {"start": v(45.5, 14) * mm, "end": v(45.5, 7) * mm});
            skCircle(sketch, "E284", {"center": v(-35.07, 7) * mm, "radius": 7 * mm, "construction": true});
            skArc(sketch, "E285", {"start": v(-35.07, 12) * mm, "mid": v(-40.07, 7) * mm, "end": v(-35.07, 2) * mm});
            skLineSegment(sketch, "E286", {"start": v(-35.07, 12) * mm, "end": v(-35.07, 14) * mm});
            skLineSegment(sketch, "E287", {"start": v(-35.07, 14) * mm, "end": v(-45.5, 14) * mm});
            skLineSegment(sketch, "E288", {"start": v(-45.5, 14) * mm, "end": v(-45.5, 0) * mm});
            skLineSegment(sketch, "E289", {"start": v(-45.5, 0) * mm, "end": v(-35.07, 0) * mm});
            skLineSegment(sketch, "E290", {"start": v(-35.07, 0) * mm, "end": v(-35.07, 2) * mm});
            skLineSegment(sketch, "E291.MirrorCS", {"start": v(45.5, 2) * mm, "end": v(-45.5, 2) * mm, "construction": true});
            skCircle(sketch, "E292", {"center": v(0, 7) * mm, "radius": 1.25 * mm, "construction": true});
            skSolve(sketch);
        }
        {
            var Q0;
            Q0=qCreatedBy(makeId("Top.planeOp"),FACE);
            var sketch = newSketch(context, id + "F13", { "sketchPlane" : qUnion([Q0])});
            skPoint(sketch, "E293.middle", {"position": v(0, 0) * mm});
            skCircle(sketch, "E294", {"center": v(0, 0) * mm, "radius": 2.5 * mm, "construction": true});
            skLineSegment(sketch, "E295.MirrorCS", {"start": v(-32.65, 17.41) * mm, "end": v(-45.5, 17.41) * mm});
            skLineSegment(sketch, "E296.MirrorCS", {"start": v(-32.65, -17.41) * mm, "end": v(-45.5, -17.41) * mm});
            skLineSegment(sketch, "E297.MirrorCS", {"start": v(-45.5, 17.41) * mm, "end": v(-45.5, -17.41) * mm});
            skArc(sketch, "E298", {"start": v(-32.65, 17.41) * mm, "mid": v(-37, 0) * mm, "end": v(-32.65, -17.41) * mm});
            skLineSegment(sketch, "E299.bottom", {"start": v(-45.5, 8.28) * mm, "end": v(-45.5, -8.52) * mm, "construction": true});
            skLineSegment(sketch, "E299.left", {"start": v(-45.5, 8.28) * mm, "end": v(-59, 8.28) * mm, "construction": true});
            skLineSegment(sketch, "E300", {"start": v(-45.5, -8.52) * mm, "end": v(-59, -8.52) * mm, "construction": true});
            skLineSegment(sketch, "E301", {"start": v(-59, -8.52) * mm, "end": v(-59, 8.28) * mm, "construction": true});
            skLineSegment(sketch, "E302", {"start": v(-45.5, 8.28) * mm, "end": v(-59, -8.52) * mm, "construction": true});
            skLineSegment(sketch, "E303", {"start": v(-45.5, -8.52) * mm, "end": v(-59, 8.28) * mm, "construction": true});
            skLineSegment(sketch, "E304", {"start": v(-52.24, 0) * mm, "end": v(-42.5, 0) * mm, "construction": true});
            skLineSegment(sketch, "E305", {"start": v(-27.2, 0) * mm, "end": v(-42.4, 0) * mm, "construction": true});
            skLineSegment(sketch, "E306.0", {"start": v(-62, -8.52) * mm, "end": v(-62, 8.28) * mm, "construction": true});
            skLineSegment(sketch, "E307", {"start": v(-45.5, 17.41) * mm, "end": v(-62, 17.41) * mm});
            skLineSegment(sketch, "E308", {"start": v(-62, 17.41) * mm, "end": v(-62, -17.41) * mm});
            skLineSegment(sketch, "E309", {"start": v(-62, -17.41) * mm, "end": v(-45.5, -17.41) * mm});
            skLineSegment(sketch, "E310.0", {"start": v(-59, -14.41) * mm, "end": v(-45.5, -14.41) * mm});
            skLineSegment(sketch, "E310.1", {"start": v(-59, 14.41) * mm, "end": v(-59, -14.41) * mm});
            skLineSegment(sketch, "E310.2", {"start": v(-45.5, 14.41) * mm, "end": v(-59, 14.41) * mm});
            skSolve(sketch);
        }
        {
            var Q0;
            Q0=qCreatedBy(id+"F4.planeOp",FACE);
            var sketch = newSketch(context, id + "F14", { "sketchPlane" : qUnion([Q0])});
            skPoint(sketch, "E311.middle", {"position": v(0, 0) * mm});
            skCircle(sketch, "E312", {"center": v(0, 0) * mm, "radius": 2.5 * mm, "construction": true});
            skLineSegment(sketch, "E313.MirrorCS", {"start": v(-32.65, 17.41) * mm, "end": v(-45.5, 17.41) * mm});
            skLineSegment(sketch, "E314.MirrorCS", {"start": v(-32.65, -17.41) * mm, "end": v(-45.5, -17.41) * mm});
            skLineSegment(sketch, "E315.MirrorCS", {"start": v(-45.5, 17.41) * mm, "end": v(-45.5, -17.41) * mm});
            skArc(sketch, "E316", {"start": v(-32.65, 17.41) * mm, "mid": v(-37, 0) * mm, "end": v(-32.65, -17.41) * mm});
            skLineSegment(sketch, "E317.bottom", {"start": v(-45.5, 8.28) * mm, "end": v(-45.5, -8.52) * mm, "construction": true});
            skLineSegment(sketch, "E317.left", {"start": v(-45.5, 8.28) * mm, "end": v(-59, 8.28) * mm, "construction": true});
            skLineSegment(sketch, "E318", {"start": v(-45.5, -8.52) * mm, "end": v(-59, -8.52) * mm, "construction": true});
            skLineSegment(sketch, "E319", {"start": v(-59, -8.52) * mm, "end": v(-59, 8.28) * mm, "construction": true});
            skLineSegment(sketch, "E320", {"start": v(-45.5, 8.28) * mm, "end": v(-59, -8.52) * mm, "construction": true});
            skLineSegment(sketch, "E321", {"start": v(-45.5, -8.52) * mm, "end": v(-59, 8.28) * mm, "construction": true});
            skLineSegment(sketch, "E322", {"start": v(-52.24, 0) * mm, "end": v(-42.5, 0) * mm, "construction": true});
            skLineSegment(sketch, "E323", {"start": v(-27.2, 0) * mm, "end": v(-42.4, 0) * mm, "construction": true});
            skLineSegment(sketch, "E324.0", {"start": v(-62, -8.52) * mm, "end": v(-62, 8.28) * mm, "construction": true});
            skLineSegment(sketch, "E325", {"start": v(-45.5, 17.41) * mm, "end": v(-62, 17.41) * mm});
            skLineSegment(sketch, "E326", {"start": v(-62, 17.41) * mm, "end": v(-62, -17.41) * mm});
            skLineSegment(sketch, "E327", {"start": v(-62, -17.41) * mm, "end": v(-45.5, -17.41) * mm});
            skLineSegment(sketch, "E328.0", {"start": v(-59, -14.41) * mm, "end": v(-45.5, -14.41) * mm});
            skLineSegment(sketch, "E328.1", {"start": v(-59, 14.41) * mm, "end": v(-59, -14.41) * mm});
            skLineSegment(sketch, "E328.2", {"start": v(-45.5, 14.41) * mm, "end": v(-59, 14.41) * mm});
            skLineSegment(sketch, "E329.0", {"start": v(-42.5, 17.41) * mm, "end": v(-42.5, -17.41) * mm});
            skSolve(sketch);
        }
        {
            var Q0;
            Q0=makeQuery(id+"F8.imprint","IMPRINT",FACE,{"disambiguationData":[TD([[makeQuery(id+"F8.imprint","IMPRINT",EDGE,{"derivedFrom":sQuery(id+"F8.wireOp",EDGE,"E1.0")}),1.0]])]});
            extrude(context, id + "F15", {"entities" : qUnion([Q0]), "depth" : 7 * mm});
        }
        {
            var Q0;
            Q0=makeQuery(id+"F8.imprint","IMPRINT",FACE,{"disambiguationData":[TD([[makeQuery(id+"F8.imprint","IMPRINT",EDGE,{"derivedFrom":sQuery(id+"F8.wireOp",EDGE,"E50")}),-1.0]])]});
            var Q1;
            Q1=makeQuery(id+"F8.imprint","IMPRINT",FACE,{"disambiguationData":[TD([[makeQuery(id+"F8.imprint","IMPRINT",EDGE,{"derivedFrom":sQuery(id+"F8.wireOp",EDGE,"E43.MirrorCS")}),-1.0]])]});
            var Q2;
            Q2=makeQuery(id+"F8.imprint","IMPRINT",FACE,{"disambiguationData":[TD([[makeQuery(id+"F8.imprint","IMPRINT",EDGE,{"derivedFrom":sQuery(id+"F8.wireOp",EDGE,"E42.MirrorCS")}),-1.0]])]});
            var Q3;
            Q3=makeQuery(id+"F8.imprint","IMPRINT",FACE,{"disambiguationData":[TD([[makeQuery(id+"F8.imprint","IMPRINT",EDGE,{"derivedFrom":sQuery(id+"F8.wireOp",EDGE,"E41.MirrorCS")}),-1.0]])]});
            var Q4;
            Q4=makeQuery(id+"F8.imprint","IMPRINT",FACE,{"disambiguationData":[TD([[makeQuery(id+"F8.imprint","IMPRINT",EDGE,{"derivedFrom":sQuery(id+"F8.wireOp",EDGE,"E40.MirrorCS")}),1.0]])]});
            var Q5;
            Q5=makeQuery(id+"F8.imprint","IMPRINT",FACE,{"disambiguationData":[TD([[makeQuery(id+"F8.imprint","IMPRINT",EDGE,{"derivedFrom":sQuery(id+"F8.wireOp",EDGE,"E39.MirrorCS")}),-1.0]])]});
            var Q6;
            Q6=makeQuery(id+"F8.imprint","IMPRINT",FACE,{"disambiguationData":[TD([[makeQuery(id+"F8.imprint","IMPRINT",EDGE,{"derivedFrom":sQuery(id+"F8.wireOp",EDGE,"E27")}),1.0]])]});
            var Q7;
            Q7=makeQuery(id+"F8.imprint","IMPRINT",FACE,{"disambiguationData":[TD([[makeQuery(id+"F8.imprint","IMPRINT",EDGE,{"derivedFrom":sQuery(id+"F8.wireOp",EDGE,"E28")}),-1.0]])]});
            var Q8;
            Q8=makeQuery(id+"F8.imprint","IMPRINT",FACE,{"disambiguationData":[TD([[makeQuery(id+"F8.imprint","IMPRINT",EDGE,{"derivedFrom":sQuery(id+"F8.wireOp",EDGE,"E29")}),1.0]])]});
            var Q9;
            Q9=makeQuery(id+"F8.imprint","IMPRINT",FACE,{"disambiguationData":[TD([[makeQuery(id+"F8.imprint","IMPRINT",EDGE,{"derivedFrom":sQuery(id+"F8.wireOp",EDGE,"E30")}),-1.0]])]});
            var Q10;
            Q10=makeQuery(id+"F8.imprint","IMPRINT",FACE,{"disambiguationData":[TD([[makeQuery(id+"F8.imprint","IMPRINT",EDGE,{"derivedFrom":sQuery(id+"F8.wireOp",EDGE,"E31")}),-1.0]])]});
            var Q11;
            Q11=makeQuery(id+"F8.imprint","IMPRINT",FACE,{"disambiguationData":[TD([[makeQuery(id+"F8.imprint","IMPRINT",EDGE,{"derivedFrom":sQuery(id+"F8.wireOp",EDGE,"E32")}),-1.0]])]});
            var Q12;
            Q12=makeQuery(id+"F8.imprint","IMPRINT",FACE,{"disambiguationData":[TD([[makeQuery(id+"F8.imprint","IMPRINT",EDGE,{"derivedFrom":sQuery(id+"F8.wireOp",EDGE,"E33")}),-1.0]])]});
            var Q13;
            Q13=makeQuery(id+"F8.imprint","IMPRINT",FACE,{"disambiguationData":[TD([[makeQuery(id+"F8.imprint","IMPRINT",EDGE,{"derivedFrom":sQuery(id+"F8.wireOp",EDGE,"E34.MirrorCS")}),-1.0]])]});
            var Q14;
            Q14=makeQuery(id+"F8.imprint","IMPRINT",FACE,{"disambiguationData":[TD([[makeQuery(id+"F8.imprint","IMPRINT",EDGE,{"derivedFrom":sQuery(id+"F8.wireOp",EDGE,"E35.MirrorCS")}),-1.0]])]});
            var Q15;
            Q15=makeQuery(id+"F8.imprint","IMPRINT",FACE,{"disambiguationData":[TD([[makeQuery(id+"F8.imprint","IMPRINT",EDGE,{"derivedFrom":sQuery(id+"F8.wireOp",EDGE,"E36.MirrorCS")}),-1.0]])]});
            var Q16;
            Q16=makeQuery(id+"F8.imprint","IMPRINT",FACE,{"disambiguationData":[TD([[makeQuery(id+"F8.imprint","IMPRINT",EDGE,{"derivedFrom":sQuery(id+"F8.wireOp",EDGE,"E37.MirrorCS")}),1.0]])]});
            var Q17;
            Q17=makeQuery(id+"F8.imprint","IMPRINT",FACE,{"disambiguationData":[TD([[makeQuery(id+"F8.imprint","IMPRINT",EDGE,{"derivedFrom":sQuery(id+"F8.wireOp",EDGE,"E38.MirrorCS")}),-1.0]])]});
            var Q18;
            Q18=makeQuery(id+"F8.imprint","IMPRINT",FACE,{"disambiguationData":[TD([[makeQuery(id+"F8.imprint","IMPRINT",EDGE,{"derivedFrom":sQuery(id+"F8.wireOp",EDGE,"E49")}),-1.0]])]});
            var Q19;
            Q19=makeQuery(id+"F8.imprint","IMPRINT",FACE,{"disambiguationData":[TD([[makeQuery(id+"F8.imprint","IMPRINT",EDGE,{"derivedFrom":sQuery(id+"F8.wireOp",EDGE,"E48.MirrorCS")}),-1.0]])]});
            var Q20;
            Q20=makeQuery(id+"F8.imprint","IMPRINT",FACE,{"disambiguationData":[TD([[makeQuery(id+"F8.imprint","IMPRINT",EDGE,{"derivedFrom":sQuery(id+"F8.wireOp",EDGE,"E47.MirrorCS")}),1.0]])]});
            var Q21;
            Q21=makeQuery(id+"F8.imprint","IMPRINT",FACE,{"disambiguationData":[TD([[makeQuery(id+"F8.imprint","IMPRINT",EDGE,{"derivedFrom":sQuery(id+"F8.wireOp",EDGE,"E46.MirrorCS")}),-1.0]])]});
            var Q22;
            Q22=makeQuery(id+"F8.imprint","IMPRINT",FACE,{"disambiguationData":[TD([[makeQuery(id+"F8.imprint","IMPRINT",EDGE,{"derivedFrom":sQuery(id+"F8.wireOp",EDGE,"E45.MirrorCS")}),-1.0]])]});
            var Q23;
            Q23=makeQuery(id+"F8.imprint","IMPRINT",FACE,{"disambiguationData":[TD([[makeQuery(id+"F8.imprint","IMPRINT",EDGE,{"derivedFrom":sQuery(id+"F8.wireOp",EDGE,"E44.MirrorCS")}),-1.0]])]});
            extrude(context, id + "F16", {"entities" : qUnion([Q0, Q1, Q2, Q3, Q4, Q5, Q6, Q7, Q8, Q9, Q10, Q11, Q12, Q13, Q14, Q15, Q16, Q17, Q18, Q19, Q20, Q21, Q22, Q23]), "operationType" : NewBodyOperationType.ADD, "depth" : 2 * mm});
        }
        {
            var Q0;
            {var subQ0=sQuery(id+"F9.wireOp",EDGE,"E164");Q0=makeQuery(id+"F9.imprint","IMPRINT",FACE,{"disambiguationData":[TD([[makeQuery(id+"F9.imprint","IMPRINT",EDGE,{"derivedFrom":subQ0}),-1.0]])]});}
            var Q1;
            {var subQ0=sQuery(id+"F9.wireOp",EDGE,"E152");Q1=makeQuery(id+"F9.imprint","IMPRINT",FACE,{"disambiguationData":[TD([[makeQuery(id+"F9.imprint","IMPRINT",EDGE,{"derivedFrom":subQ0}),1.0]])]});}
            var Q2;
            Q2=sQuery(id+"F9.wireOp",EDGE,"E161");
            revolve(context, id + "F17", {"operationType" : NewBodyOperationType.ADD, "entities" : qUnion([Q0, Q1]), "axis" : qUnion([Q2]), "revolveType" : RevolveType.SYMMETRIC, "angle" : 315 * degree});
        }
        {
            var Q0;
            {var subQ3=sQuery(id+"F9.wireOp",EDGE,"E157");Q0=makeQuery(id+"F9.imprint","IMPRINT",FACE,{"disambiguationData":[TD([[makeQuery(id+"F9.imprint","IMPRINT",EDGE,{"derivedFrom":subQ3}),1.0]])]});}
            var Q1;
            Q1=makeQuery(id+"F9.imprint","IMPRINT",FACE,{"disambiguationData":[TD([[makeQuery(id+"F9.imprint","IMPRINT",EDGE,{"derivedFrom":sQuery(id+"F9.wireOp",EDGE,"E158")}),-1.0]])]});
            var Q2;
            Q2=sQuery(id+"F9.wireOp",EDGE,"E161");
            revolve(context, id + "F18", {"operationType" : NewBodyOperationType.ADD, "entities" : qUnion([Q0, Q1]), "axis" : qUnion([Q2]), "revolveType" : RevolveType.FULL});
        }
        {
            var Q0;
            Q0=makeQuery(id+"F12.imprint","IMPRINT",FACE,{"disambiguationData":[TD([[makeQuery(id+"F12.imprint","IMPRINT",EDGE,{"derivedFrom":sQuery(id+"F12.wireOp",EDGE,"E285")}),-1.0]])]});
            extrude(context, id + "F19", {"entities" : qUnion([Q0]), "operationType" : NewBodyOperationType.ADD, "depth" : 2.5 * mm});
        }
        {
            var Q0;
            Q0=makeQuery(id+"F11.imprint","IMPRINT",FACE,{"disambiguationData":[TD([[makeQuery(id+"F11.imprint","IMPRINT",EDGE,{"derivedFrom":sQuery(id+"F11.wireOp",EDGE,"E259")}),-1.0]])]});
            extrude(context, id + "F20", {"entities" : qUnion([Q0]), "operationType" : NewBodyOperationType.ADD, "oppositeDirection" : true, "depth" : 2.5 * mm});
        }
        {
            var Q0;
            Q0=makeQuery(id+"F13.imprint","IMPRINT",FACE,{"disambiguationData":[TD([[makeQuery(id+"F13.imprint","IMPRINT",EDGE,{"derivedFrom":sQuery(id+"F13.wireOp",EDGE,"E295.MirrorCS")}),1.0]])]});
            var Q1;
            {var subQ1=sQuery(id+"F13.wireOp",EDGE,"E299.bottom");Q1=makeQuery(id+"F13.imprint","IMPRINT",FACE,{"disambiguationData":[TD([[makeQuery(id+"F13.imprint","IMPRINT",EDGE,{"derivedFrom":subQ1}),1.0]])]});}
            var Q2;
            {var subQ5=sQuery(id+"F13.wireOp",EDGE,"E301");Q2=makeQuery(id+"F13.imprint","IMPRINT",FACE,{"disambiguationData":[TD([[makeQuery(id+"F13.imprint","IMPRINT",EDGE,{"derivedFrom":subQ5}),-1.0]])]});}
            var Q3;
            {var subQ0=sQuery(id+"F13.wireOp",EDGE,"E310.0");Q3=makeQuery(id+"F13.imprint","IMPRINT",FACE,{"disambiguationData":[TD([[makeQuery(id+"F13.imprint","IMPRINT",EDGE,{"derivedFrom":subQ0}),1.0]])]});}
            extrude(context, id + "F21", {"entities" : qUnion([Q0, Q1, Q2, Q3]), "operationType" : NewBodyOperationType.ADD, "depth" : 2.5 * mm});
        }
        {
            var Q0;
            {var subQ3=sQuery(id+"F14.wireOp",EDGE,"E313.MirrorCS");Q0=makeQuery(id+"F14.imprint","IMPRINT",FACE,{"disambiguationData":[TD([[makeQuery(id+"F14.imprint","IMPRINT",EDGE,{"derivedFrom":subQ3}),1.0]])]});}
            var Q1;
            {var subQ7=sQuery(id+"F14.wireOp",EDGE,"E329.0");Q1=makeQuery(id+"F14.imprint","IMPRINT",FACE,{"disambiguationData":[TD([[makeQuery(id+"F14.imprint","IMPRINT",EDGE,{"derivedFrom":subQ7}),-1.0]])]});}
            extrude(context, id + "F22", {"entities" : qUnion([Q0, Q1]), "operationType" : NewBodyOperationType.ADD, "oppositeDirection" : true, "depth" : 2.5 * mm});
        }
        {
            var Q0;
            {var subQ4=sQuery(id+"F13.wireOp",EDGE,"E301");Q0=makeQuery(id+"F13.imprint","IMPRINT",FACE,{"disambiguationData":[TD([[makeQuery(id+"F13.imprint","IMPRINT",EDGE,{"derivedFrom":subQ4}),1.0]])]});}
            var Q1;
            {var subQ0=sQuery(id+"F13.wireOp",EDGE,"6jEM1cKR-Vwea-ILg7-sG8q-rrc46WkZxeoR");Q1=makeQuery(id+"F13.imprint","IMPRINT",FACE,{"disambiguationData":[TD([[makeQuery(id+"F13.imprint","IMPRINT",EDGE,{"derivedFrom":subQ0}),-1.0]])]});}
            var Q2;
            {var subQ0=sQuery(id+"F13.wireOp",EDGE,"E307");Q2=makeQuery(id+"F13.imprint","IMPRINT",FACE,{"disambiguationData":[TD([[makeQuery(id+"F13.imprint","IMPRINT",EDGE,{"derivedFrom":subQ0}),1.0]])]});}
            extrude(context, id + "F23", {"entities" : qUnion([Q0, Q1, Q2]), "operationType" : NewBodyOperationType.ADD, "depth" : 14 * mm});
        }
        {
            var Q0;
            {var subQ0=sQuery(id+"F14.wireOp",EDGE,"E325");Q0=makeQuery(id+"F14.imprint","IMPRINT",FACE,{"disambiguationData":[TD([[makeQuery(id+"F14.imprint","IMPRINT",EDGE,{"derivedFrom":subQ0}),1.0]])]});}
            extrude(context, id + "F24", {"entities" : qUnion([Q0]), "operationType" : NewBodyOperationType.ADD, "depth" : 48.17 * mm});
        }
        {
            var Q0;
            Q0=makeQuery(id+"F10.imprint","IMPRINT",FACE,{"disambiguationData":[TD([[makeQuery(id+"F10.imprint","IMPRINT",EDGE,{"derivedFrom":sQuery(id+"F10.wireOp",EDGE,"E204")}),-1.0]])]});
            var Q1;
            {var subQ0=sQuery(id+"F10.wireOp",EDGE,"6a0bf37f-b3f9-4be4-bbcd-48762ca18b15");Q1=makeQuery(id+"F10.imprint","IMPRINT",FACE,{"disambiguationData":[TD([[makeQuery(id+"F10.imprint","IMPRINT",EDGE,{"derivedFrom":subQ0}),-1.0]])]});}
            var Q2;
            Q2=makeQuery(id+"F10.imprint","IMPRINT",FACE,{"disambiguationData":[TD([[makeQuery(id+"F10.imprint","IMPRINT",EDGE,{"derivedFrom":sQuery(id+"F10.wireOp",EDGE,"E204")}),1.0]])]});
            var Q3;
            Q3=makeQuery(id+"F10.imprint","IMPRINT",FACE,{"disambiguationData":[TD([[makeQuery(id+"F10.imprint","IMPRINT",EDGE,{"derivedFrom":sQuery(id+"F10.wireOp",EDGE,"E205.1")}),-1.0]])]});
            var Q4;
            {var subQ0=sQuery(id+"F10.wireOp",EDGE,"36538cae-b972-4159-a8ab-ed7d0897e562");Q4=makeQuery(id+"F10.imprint","IMPRINT",FACE,{"disambiguationData":[TD([[makeQuery(id+"F10.imprint","IMPRINT",EDGE,{"derivedFrom":subQ0}),1.0]])]});}
            var Q5;
            Q5=makeQuery(id+"F10.imprint","IMPRINT",FACE,{"disambiguationData":[TD([[makeQuery(id+"F10.imprint","IMPRINT",EDGE,{"derivedFrom":sQuery(id+"F10.wireOp",EDGE,"E203.MirrorCS")}),-1.0]])]});
            var Q6;
            Q6=makeQuery(id+"F10.imprint","IMPRINT",FACE,{"disambiguationData":[TD([[makeQuery(id+"F10.imprint","IMPRINT",EDGE,{"derivedFrom":sQuery(id+"F10.wireOp",EDGE,"E202.0")}),1.0]])]});
            var Q7;
            {var subQ2=sQuery(id+"F10.wireOp",EDGE,"E232.MirrorCS");Q7=makeQuery(id+"F10.imprint","IMPRINT",FACE,{"disambiguationData":[TD([[makeQuery(id+"F10.imprint","IMPRINT",EDGE,{"derivedFrom":subQ2}),1.0]])]});}
            var Q8;
            {var subQ0=sQuery(id+"F10.wireOp",EDGE,"E215");Q8=makeQuery(id+"F10.imprint","IMPRINT",FACE,{"disambiguationData":[TD([[makeQuery(id+"F10.imprint","IMPRINT",EDGE,{"derivedFrom":subQ0}),-1.0]])]});}
            var Q9;
            {var subQ2=sQuery(id+"F10.wireOp",EDGE,"E230");Q9=makeQuery(id+"F10.imprint","IMPRINT",FACE,{"disambiguationData":[TD([[makeQuery(id+"F10.imprint","IMPRINT",EDGE,{"derivedFrom":subQ2}),-1.0]])]});}
            extrude(context, id + "F25", {"entities" : qUnion([Q0, Q1, Q2, Q3, Q4, Q5, Q6, Q7, Q8, Q9]), "operationType" : NewBodyOperationType.ADD, "oppositeDirection" : true, "depth" : 3 * mm});
        }
        {
            var Q0;
            {var subQ1=sQuery(id+"F10.wireOp",EDGE,"E223.MirrorCS");Q0=makeQuery(id+"F10.imprint","IMPRINT",FACE,{"disambiguationData":[TD([[makeQuery(id+"F10.imprint","IMPRINT",EDGE,{"derivedFrom":subQ1}),-1.0]])]});}
            var Q1;
            {var subQ0=sQuery(id+"F10.wireOp",EDGE,"E229");var subQ1=sQuery(id+"F10.wireOp",EDGE,"E219");var subQ2=makeQuery(id+"F10.imprint","INTERSECT",VERTEX,{"disambiguationData":[OD(0.0)],"derivedFrom":[subQ1,subQ0]});Q1=makeQuery(id+"F10.imprint","IMPRINT",FACE,{"disambiguationData":[TD([[makeQuery(id+"F10.imprint","IMPRINT",EDGE,{"disambiguationData":[TD([[subQ2,-1.0]])],"derivedFrom":subQ1}),-1.0]])]});}
            var Q2;
            {var subQ0=sQuery(id+"F10.wireOp",EDGE,"E229");var subQ1=sQuery(id+"F10.wireOp",EDGE,"E219");var subQ2=makeQuery(id+"F10.imprint","INTERSECT",VERTEX,{"disambiguationData":[OD(1.0)],"derivedFrom":[subQ1,subQ0]});Q2=makeQuery(id+"F10.imprint","IMPRINT",FACE,{"disambiguationData":[TD([[makeQuery(id+"F10.imprint","IMPRINT",EDGE,{"disambiguationData":[TD([[subQ2,1.0]])],"derivedFrom":subQ1}),-1.0]])]});}
            var Q3;
            {var subQ0=sQuery(id+"F10.wireOp",EDGE,"E222.1");Q3=makeQuery(id+"F10.imprint","IMPRINT",FACE,{"disambiguationData":[TD([[makeQuery(id+"F10.imprint","IMPRINT",EDGE,{"derivedFrom":subQ0}),1.0]])]});}
            var Q4;
            Q4=makeQuery(id+"F10.imprint","IMPRINT",FACE,{"disambiguationData":[TD([[makeQuery(id+"F10.imprint","IMPRINT",EDGE,{"derivedFrom":sQuery(id+"F10.wireOp",EDGE,"E202.0")}),-1.0]])]});
            extrude(context, id + "F26", {"entities" : qUnion([Q0, Q1, Q2, Q3, Q4]), "operationType" : NewBodyOperationType.ADD, "endBound" : BoundingType.SYMMETRIC, "depth" : 3 * mm});
        }
        {
            var Q0;
            {var subQ0=sQuery(id+"F10.wireOp",EDGE,"E229");var subQ1=sQuery(id+"F10.wireOp",EDGE,"E219");var subQ2=makeQuery(id+"F10.imprint","INTERSECT",VERTEX,{"disambiguationData":[OD(1.0)],"derivedFrom":[subQ1,subQ0]});Q0=makeQuery(id+"F10.imprint","IMPRINT",FACE,{"disambiguationData":[TD([[makeQuery(id+"F10.imprint","IMPRINT",EDGE,{"disambiguationData":[TD([[subQ2,1.0]])],"derivedFrom":subQ1}),-1.0]])]});}
            var Q1;
            {var subQ0=sQuery(id+"F10.wireOp",EDGE,"E229");var subQ1=sQuery(id+"F10.wireOp",EDGE,"E219");var subQ2=makeQuery(id+"F10.imprint","INTERSECT",VERTEX,{"disambiguationData":[OD(0.0)],"derivedFrom":[subQ1,subQ0]});Q1=makeQuery(id+"F10.imprint","IMPRINT",FACE,{"disambiguationData":[TD([[makeQuery(id+"F10.imprint","IMPRINT",EDGE,{"disambiguationData":[TD([[subQ2,-1.0]])],"derivedFrom":subQ1}),-1.0]])]});}
            extrude(context, id + "F27", {"entities" : qUnion([Q0, Q1]), "operationType" : NewBodyOperationType.ADD, "depth" : 3.5 * mm});
        }
        {
            var Q0;
            Q0=makeQuery(id+"F10.imprint","IMPRINT",FACE,{"disambiguationData":[TD([[makeQuery(id+"F10.imprint","IMPRINT",EDGE,{"derivedFrom":sQuery(id+"F10.wireOp",EDGE,"E203.MirrorCS")}),-1.0]])]});
            var Q1;
            Q1=makeQuery(id+"F10.imprint","IMPRINT",FACE,{"disambiguationData":[TD([[makeQuery(id+"F10.imprint","IMPRINT",EDGE,{"derivedFrom":sQuery(id+"F10.wireOp",EDGE,"E204")}),1.0]])]});
            var Q2;
            Q2=makeQuery(id+"F10.imprint","IMPRINT",FACE,{"disambiguationData":[TD([[makeQuery(id+"F10.imprint","IMPRINT",EDGE,{"derivedFrom":sQuery(id+"F10.wireOp",EDGE,"E202.0")}),1.0]])]});
            var Q3;
            Q3=makeQuery(id+"F10.imprint","IMPRINT",FACE,{"disambiguationData":[TD([[makeQuery(id+"F10.imprint","IMPRINT",EDGE,{"derivedFrom":sQuery(id+"F10.wireOp",EDGE,"E205.1")}),-1.0]])]});
            extrude(context, id + "F28", {"entities" : qUnion([Q0, Q1, Q2, Q3]), "operationType" : NewBodyOperationType.ADD, "depth" : 8.2 * mm});
        }
        {
            var Q0;
            Q0=qCreatedBy(id+"F6.planeOp",FACE);
            var sketch = newSketch(context, id + "F29", { "sketchPlane" : qUnion([Q0])});
            skCircle(sketch, "E330", {"center": v(0, 0) * mm, "radius": 1.5 * mm, "construction": true});
            skCircle(sketch, "E331", {"center": v(0, 55.8) * mm, "radius": 1.25 * mm, "construction": true});
            skLineSegment(sketch, "E332", {"start": v(0, 55.8) * mm, "end": v(0, 14) * mm, "construction": true});
            skSolve(sketch);
        }
        {
            var Q0;
            Q0=qCreatedBy(id+"F5.planeOp",FACE);
            var sketch = newSketch(context, id + "F30", { "sketchPlane" : qUnion([Q0])});
            skPoint(sketch, "E333.middle", {"position": v(0, 0) * mm});
            skCircle(sketch, "E334", {"center": v(0, 0) * mm, "radius": 1.5 * mm, "construction": true});
            skLineSegment(sketch, "E335.bottom", {"start": v(-45.5, 8.28) * mm, "end": v(-45.5, -8.52) * mm, "construction": true});
            skLineSegment(sketch, "E335.left", {"start": v(-45.5, 8.28) * mm, "end": v(-59, 8.28) * mm, "construction": true});
            skLineSegment(sketch, "E336", {"start": v(-45.5, -8.52) * mm, "end": v(-59, -8.52) * mm, "construction": true});
            skLineSegment(sketch, "E337", {"start": v(-59, -8.52) * mm, "end": v(-59, 8.28) * mm, "construction": true});
            skLineSegment(sketch, "E338", {"start": v(-45.5, 8.28) * mm, "end": v(-59, -8.52) * mm, "construction": true});
            skLineSegment(sketch, "E339", {"start": v(-45.5, -8.52) * mm, "end": v(-59, 8.28) * mm, "construction": true});
            skLineSegment(sketch, "E340", {"start": v(-52.24, 0) * mm, "end": v(-42.5, 0) * mm, "construction": true});
            skLineSegment(sketch, "E341", {"start": v(-27.2, 0) * mm, "end": v(-42.4, 0) * mm, "construction": true});
            skLineSegment(sketch, "E342.0", {"start": v(-62, -8.52) * mm, "end": v(-62, 8.28) * mm, "construction": true});
            skLineSegment(sketch, "E343", {"start": v(-62, 17.41) * mm, "end": v(-62, -17.41) * mm});
            skLineSegment(sketch, "E344.0", {"start": v(-59, -14.41) * mm, "end": v(-45.5, -14.41) * mm, "construction": true});
            skLineSegment(sketch, "E344.1", {"start": v(-59, 14.41) * mm, "end": v(-59, -14.41) * mm});
            skLineSegment(sketch, "E344.2", {"start": v(-45.5, 14.41) * mm, "end": v(-59, 14.41) * mm, "construction": true});
            skLineSegment(sketch, "E345.0", {"start": v(-42.5, 17.41) * mm, "end": v(-42.5, -17.41) * mm});
            skLineSegment(sketch, "E346", {"start": v(-62, 17.41) * mm, "end": v(-42.5, 17.41) * mm});
            skLineSegment(sketch, "E347", {"start": v(-42.5, -17.41) * mm, "end": v(-62, -17.41) * mm});
            skLineSegment(sketch, "E348", {"start": v(-45.5, 14.41) * mm, "end": v(-45.5, -14.41) * mm});
            skLineSegment(sketch, "E349", {"start": v(-62, 14.41) * mm, "end": v(-42.5, 14.41) * mm});
            skLineSegment(sketch, "E350", {"start": v(-42.5, -14.41) * mm, "end": v(-62, -14.41) * mm});
            skPoint(sketch, "E350.endSnap0", {"position": v(-52.25, -14.41) * mm});
            skSolve(sketch);
        }
        {
            var Q0;
            Q0=qCreatedBy(id+"F7.planeOp",FACE);
            var sketch = newSketch(context, id + "F31", { "sketchPlane" : qUnion([Q0])});
            skPoint(sketch, "E351.middle", {"position": v(-3, 0) * mm});
            skLineSegment(sketch, "E352.bottom", {"start": v(-48.5, 8.28) * mm, "end": v(-48.5, -8.52) * mm, "construction": true});
            skLineSegment(sketch, "E352.left", {"start": v(-48.5, 8.28) * mm, "end": v(-62, 8.28) * mm, "construction": true});
            skLineSegment(sketch, "E353", {"start": v(-48.5, -8.52) * mm, "end": v(-62, -8.52) * mm, "construction": true});
            skLineSegment(sketch, "E354", {"start": v(-62, -8.52) * mm, "end": v(-62, 8.28) * mm, "construction": true});
            skLineSegment(sketch, "E355", {"start": v(-48.5, 8.28) * mm, "end": v(-62, -8.52) * mm, "construction": true});
            skLineSegment(sketch, "E356", {"start": v(-48.5, -8.52) * mm, "end": v(-62, 8.28) * mm, "construction": true});
            skLineSegment(sketch, "E357", {"start": v(-55.24, 0) * mm, "end": v(-45.5, 0) * mm, "construction": true});
            skLineSegment(sketch, "E358", {"start": v(-30.2, 0) * mm, "end": v(-45.4, 0) * mm, "construction": true});
            skLineSegment(sketch, "E359.0", {"start": v(-65, -8.52) * mm, "end": v(-65, 8.28) * mm, "construction": true});
            skLineSegment(sketch, "E360", {"start": v(-65, 17.41) * mm, "end": v(-65, -17.41) * mm});
            skLineSegment(sketch, "E361.0", {"start": v(-62, -14.41) * mm, "end": v(-48.5, -14.41) * mm, "construction": true});
            skLineSegment(sketch, "E361.1", {"start": v(-62, 14.41) * mm, "end": v(-62, -14.41) * mm});
            skLineSegment(sketch, "E361.2", {"start": v(-48.5, 14.41) * mm, "end": v(-62, 14.41) * mm, "construction": true});
            skLineSegment(sketch, "E362.0", {"start": v(-45.5, 17.41) * mm, "end": v(-45.5, -17.41) * mm});
            skLineSegment(sketch, "E363", {"start": v(-65, 17.41) * mm, "end": v(-45.5, 17.41) * mm});
            skLineSegment(sketch, "E364", {"start": v(-45.5, -17.41) * mm, "end": v(-65, -17.41) * mm});
            skCircle(sketch, "E365", {"center": v(0, 0) * mm, "radius": 3 * mm, "construction": true});
            skLineSegment(sketch, "E366", {"start": v(-48.5, 14.41) * mm, "end": v(-48.5, -14.41) * mm});
            skLineSegment(sketch, "E367", {"start": v(-65, 14.41) * mm, "end": v(-45.5, 14.41) * mm});
            skLineSegment(sketch, "E368", {"start": v(-45.5, -14.41) * mm, "end": v(-65, -14.41) * mm});
            skSolve(sketch);
        }
        {
            var Q0;
            Q0=sQuery(id+"F29.wireOp",VERTEX,"E332.start");
            var Q1;
            Q1=makeQuery(id+"F15.opExtrude","SWEPT_BODY",BODY,{"disambiguationData":[OSD([sQuery(id+"F8.wireOp",EDGE,"E1.0"),sQuery(id+"F8.wireOp",EDGE,"E27"),sQuery(id+"F8.wireOp",EDGE,"E28"),sQuery(id+"F8.wireOp",EDGE,"E29"),sQuery(id+"F8.wireOp",EDGE,"E30"),sQuery(id+"F8.wireOp",EDGE,"E31"),sQuery(id+"F8.wireOp",EDGE,"E32"),sQuery(id+"F8.wireOp",EDGE,"E33"),sQuery(id+"F8.wireOp",EDGE,"E34.MirrorCS"),sQuery(id+"F8.wireOp",EDGE,"E35.MirrorCS"),sQuery(id+"F8.wireOp",EDGE,"E36.MirrorCS"),sQuery(id+"F8.wireOp",EDGE,"E37.MirrorCS"),sQuery(id+"F8.wireOp",EDGE,"E38.MirrorCS"),sQuery(id+"F8.wireOp",EDGE,"E39.MirrorCS"),sQuery(id+"F8.wireOp",EDGE,"E40.MirrorCS"),sQuery(id+"F8.wireOp",EDGE,"E41.MirrorCS"),sQuery(id+"F8.wireOp",EDGE,"E42.MirrorCS"),sQuery(id+"F8.wireOp",EDGE,"E43.MirrorCS"),sQuery(id+"F8.wireOp",EDGE,"E44.MirrorCS"),sQuery(id+"F8.wireOp",EDGE,"E45.MirrorCS"),sQuery(id+"F8.wireOp",EDGE,"E46.MirrorCS"),sQuery(id+"F8.wireOp",EDGE,"E47.MirrorCS"),sQuery(id+"F8.wireOp",EDGE,"E48.MirrorCS"),sQuery(id+"F8.wireOp",EDGE,"E49"),sQuery(id+"F8.wireOp",EDGE,"E50"),sQuery(id+"F8.wireOp",EDGE,"E51"),sQuery(id+"F8.wireOp",EDGE,"E52"),sQuery(id+"F8.wireOp",EDGE,"E53"),sQuery(id+"F8.wireOp",EDGE,"E54"),sQuery(id+"F8.wireOp",EDGE,"E55"),sQuery(id+"F8.wireOp",EDGE,"E56"),sQuery(id+"F8.wireOp",EDGE,"E57"),sQuery(id+"F8.wireOp",EDGE,"E58.MirrorCS"),sQuery(id+"F8.wireOp",EDGE,"E59.MirrorCS"),sQuery(id+"F8.wireOp",EDGE,"E60.MirrorCS"),sQuery(id+"F8.wireOp",EDGE,"E61.MirrorCS"),sQuery(id+"F8.wireOp",EDGE,"E62.MirrorCS"),sQuery(id+"F8.wireOp",EDGE,"E63.MirrorCS"),sQuery(id+"F8.wireOp",EDGE,"E64.MirrorCS"),sQuery(id+"F8.wireOp",EDGE,"E65.MirrorCS"),sQuery(id+"F8.wireOp",EDGE,"E66.MirrorCS"),sQuery(id+"F8.wireOp",EDGE,"E67.MirrorCS"),sQuery(id+"F8.wireOp",EDGE,"E68.MirrorCS"),sQuery(id+"F8.wireOp",EDGE,"E69.MirrorCS"),sQuery(id+"F8.wireOp",EDGE,"E70.MirrorCS"),sQuery(id+"F8.wireOp",EDGE,"E71.MirrorCS"),sQuery(id+"F8.wireOp",EDGE,"E72.MirrorCS"),sQuery(id+"F8.wireOp",EDGE,"E73"),sQuery(id+"F8.wireOp",EDGE,"E74"),sQuery(id+"F8.wireOp",EDGE,"E76"),sQuery(id+"F8.wireOp",EDGE,"E78"),sQuery(id+"F8.wireOp",EDGE,"E80"),sQuery(id+"F8.wireOp",EDGE,"E82"),sQuery(id+"F8.wireOp",EDGE,"E84"),sQuery(id+"F8.wireOp",EDGE,"E86"),sQuery(id+"F8.wireOp",EDGE,"E88"),sQuery(id+"F8.wireOp",EDGE,"E90"),sQuery(id+"F8.wireOp",EDGE,"E92"),sQuery(id+"F8.wireOp",EDGE,"E94"),sQuery(id+"F8.wireOp",EDGE,"E96"),sQuery(id+"F8.wireOp",EDGE,"E98"),sQuery(id+"F8.wireOp",EDGE,"E100"),sQuery(id+"F8.wireOp",EDGE,"E102"),sQuery(id+"F8.wireOp",EDGE,"E104"),sQuery(id+"F8.wireOp",EDGE,"E106"),sQuery(id+"F8.wireOp",EDGE,"E108"),sQuery(id+"F8.wireOp",EDGE,"E110"),sQuery(id+"F8.wireOp",EDGE,"E112"),sQuery(id+"F8.wireOp",EDGE,"E114"),sQuery(id+"F8.wireOp",EDGE,"E116"),sQuery(id+"F8.wireOp",EDGE,"E118"),sQuery(id+"F8.wireOp",EDGE,"E119"),sQuery(id+"F8.wireOp",EDGE,"E122"),sQuery(id+"F8.wireOp",EDGE,"E124"),sQuery(id+"F8.wireOp",EDGE,"E125"),sQuery(id+"F8.wireOp",EDGE,"E126"),sQuery(id+"F8.wireOp",EDGE,"E127"),sQuery(id+"F8.wireOp",EDGE,"E128"),sQuery(id+"F8.wireOp",EDGE,"E129"),sQuery(id+"F8.wireOp",EDGE,"E130"),sQuery(id+"F8.wireOp",EDGE,"E131"),sQuery(id+"F8.wireOp",EDGE,"E132"),sQuery(id+"F8.wireOp",EDGE,"E133"),sQuery(id+"F8.wireOp",EDGE,"E134"),sQuery(id+"F8.wireOp",EDGE,"E135"),sQuery(id+"F8.wireOp",EDGE,"E136"),sQuery(id+"F8.wireOp",EDGE,"E137"),sQuery(id+"F8.wireOp",EDGE,"E138"),sQuery(id+"F8.wireOp",EDGE,"E139"),sQuery(id+"F8.wireOp",EDGE,"E140"),sQuery(id+"F8.wireOp",EDGE,"E141"),sQuery(id+"F8.wireOp",EDGE,"E142"),sQuery(id+"F8.wireOp",EDGE,"E143"),sQuery(id+"F8.wireOp",EDGE,"E144"),sQuery(id+"F8.wireOp",EDGE,"E145"),sQuery(id+"F8.wireOp",EDGE,"E146"),sQuery(id+"F8.wireOp",EDGE,"E147")])]});
            hole(context, id + "F32", {"style" : HoleStyle.SIMPLE, "endStyle" : HoleEndStyle.BLIND, "oppositeDirection" : true, "holeDiameter" : 7 * mm, "holeDepth" : 4 * mm, "isTappedThrough" : true, "tappedDepth" : 12 * mm, "tapClearance" : 3, "startFromSketch" : true, "locations" : qUnion([Q0]), "scope" : qUnion([Q1])});
        }
        {
            var Q0;
            {var subQ4=sQuery(id+"F30.wireOp",EDGE,"E347");Q0=makeQuery(id+"F30.imprint","IMPRINT",FACE,{"disambiguationData":[TD([[makeQuery(id+"F30.imprint","IMPRINT",EDGE,{"derivedFrom":subQ4}),-1.0]])]});}
            var Q1;
            {var subQ4=sQuery(id+"F31.wireOp",EDGE,"E364");Q1=makeQuery(id+"F31.imprint","IMPRINT",FACE,{"disambiguationData":[TD([[makeQuery(id+"F31.imprint","IMPRINT",EDGE,{"derivedFrom":subQ4}),-1.0]])]});}
            loft(context, id + "F33", {"sheetProfilesArray" : [{ "sheetProfileEntities" : qUnion([Q0]) }, { "sheetProfileEntities" : qUnion([Q1]) }]});
        }
        {
            var Q1;
            {var subQ5=sQuery(id+"F30.wireOp",EDGE,"E348");Q1=makeQuery(id+"F30.imprint","IMPRINT",FACE,{"disambiguationData":[TD([[makeQuery(id+"F30.imprint","IMPRINT",EDGE,{"derivedFrom":subQ5}),1.0]])]});}
            var Q2;
            {var subQ5=sQuery(id+"F31.wireOp",EDGE,"E366");Q2=makeQuery(id+"F31.imprint","IMPRINT",FACE,{"disambiguationData":[TD([[makeQuery(id+"F31.imprint","IMPRINT",EDGE,{"derivedFrom":subQ5}),1.0]])]});}
            loft(context, id + "F34", {"operationType" : NewBodyOperationType.ADD, "sheetProfilesArray" : [{ "sheetProfileEntities" : qUnion([Q1]) }, { "sheetProfileEntities" : qUnion([Q2]) }]});
        }
        {
            var Q1;
            {var subQ0=sQuery(id+"F30.wireOp",EDGE,"E346");Q1=makeQuery(id+"F30.imprint","IMPRINT",FACE,{"disambiguationData":[TD([[makeQuery(id+"F30.imprint","IMPRINT",EDGE,{"derivedFrom":subQ0}),-1.0]])]});}
            var Q2;
            {var subQ0=sQuery(id+"F31.wireOp",EDGE,"E363");Q2=makeQuery(id+"F31.imprint","IMPRINT",FACE,{"disambiguationData":[TD([[makeQuery(id+"F31.imprint","IMPRINT",EDGE,{"derivedFrom":subQ0}),-1.0]])]});}
            loft(context, id + "F35", {"operationType" : NewBodyOperationType.ADD, "sheetProfilesArray" : [{ "sheetProfileEntities" : qUnion([Q1]) }, { "sheetProfileEntities" : qUnion([Q2]) }]});
        }
        {
            var Q1;
            {var subQ5=sQuery(id+"F30.wireOp",EDGE,"E344.1");Q1=makeQuery(id+"F30.imprint","IMPRINT",FACE,{"disambiguationData":[TD([[makeQuery(id+"F30.imprint","IMPRINT",EDGE,{"derivedFrom":subQ5}),-1.0]])]});}
            var Q2;
            {var subQ5=sQuery(id+"F31.wireOp",EDGE,"E361.1");Q2=makeQuery(id+"F31.imprint","IMPRINT",FACE,{"disambiguationData":[TD([[makeQuery(id+"F31.imprint","IMPRINT",EDGE,{"derivedFrom":subQ5}),-1.0]])]});}
            loft(context, id + "F36", {"operationType" : NewBodyOperationType.ADD, "sheetProfilesArray" : [{ "sheetProfileEntities" : qUnion([Q1]) }, { "sheetProfileEntities" : qUnion([Q2]) }]});
        }
        {
            var Q0;
            {var subQ0=sQuery(id+"F31.wireOp",EDGE,"E363");Q0=makeQuery(id+"F31.imprint","IMPRINT",FACE,{"disambiguationData":[TD([[makeQuery(id+"F31.imprint","IMPRINT",EDGE,{"derivedFrom":subQ0}),-1.0]])]});}
            var Q1;
            {var subQ5=sQuery(id+"F31.wireOp",EDGE,"E366");Q1=makeQuery(id+"F31.imprint","IMPRINT",FACE,{"disambiguationData":[TD([[makeQuery(id+"F31.imprint","IMPRINT",EDGE,{"derivedFrom":subQ5}),1.0]])]});}
            var Q2;
            {var subQ4=sQuery(id+"F31.wireOp",EDGE,"E364");Q2=makeQuery(id+"F31.imprint","IMPRINT",FACE,{"disambiguationData":[TD([[makeQuery(id+"F31.imprint","IMPRINT",EDGE,{"derivedFrom":subQ4}),-1.0]])]});}
            var Q3;
            {var subQ5=sQuery(id+"F31.wireOp",EDGE,"E361.1");Q3=makeQuery(id+"F31.imprint","IMPRINT",FACE,{"disambiguationData":[TD([[makeQuery(id+"F31.imprint","IMPRINT",EDGE,{"derivedFrom":subQ5}),-1.0]])]});}
            extrude(context, id + "F37", {"entities" : qUnion([Q0, Q1, Q2, Q3]), "operationType" : NewBodyOperationType.ADD, "depth" : 8 * mm});
        }
        {
            var Q0;
            {var subQ0=sQuery(id+"F8.wireOp",EDGE,"E145");var subQ1=sQuery(id+"F8.wireOp",EDGE,"E69.MirrorCS");var subQ2=sQuery(id+"F8.wireOp",EDGE,"E46.MirrorCS");var subQ3=makeQuery(id+"F16.opExtrude","CAP_FACE",FACE,{"disambiguationData":[OSD([subQ2,subQ1,sQuery(id+"F8.wireOp",EDGE,"E117"),subQ0])],"isStart":true});var subQ4=sQuery(id+"F12.wireOp",EDGE,"E290");var subQ5=sQuery(id+"F12.wireOp",EDGE,"E289");var subQ6=sQuery(id+"F12.wireOp",EDGE,"E288");var subQ7=sQuery(id+"F12.wireOp",EDGE,"E287");var subQ8=sQuery(id+"F12.wireOp",EDGE,"E286");var subQ9=sQuery(id+"F12.wireOp",EDGE,"E285");var subQ10=makeQuery(id+"F19.opExtrude","CAP_FACE",FACE,{"disambiguationData":[OSD([subQ9,subQ8,subQ7,subQ6,subQ5,subQ4])],"isStart":false});var subQ11=sQuery(id+"F8.wireOp",EDGE,"E146");var subQ12=sQuery(id+"F8.wireOp",EDGE,"E68.MirrorCS");var subQ13=sQuery(id+"F8.wireOp",EDGE,"E45.MirrorCS");var subQ14=makeQuery(id+"F16.opExtrude","CAP_FACE",FACE,{"disambiguationData":[OSD([subQ13,subQ12,sQuery(id+"F8.wireOp",EDGE,"E120"),subQ11])],"isStart":true});var subQ15=makeQuery(id+"F18.opRevolve","SWEPT_FACE",FACE,{"disambiguationData":[OSD([sQuery(id+"F9.wireOp",EDGE,"E157")])]});var subQ16=sQuery(id+"F8.wireOp",EDGE,"E147");var subQ17=sQuery(id+"F8.wireOp",EDGE,"E74");var subQ18=sQuery(id+"F8.wireOp",EDGE,"E44.MirrorCS");var subQ19=makeQuery(id+"F16.opExtrude","CAP_FACE",FACE,{"disambiguationData":[OSD([subQ18,subQ17,sQuery(id+"F8.wireOp",EDGE,"E121"),subQ16])],"isStart":true});var subQ20=sQuery(id+"F9.wireOp",EDGE,"E164");var subQ21=sQuery(id+"F9.wireOp",EDGE,"E152");var subQ22=sQuery(id+"F9.wireOp",EDGE,"E151");var subQ23=sQuery(id+"F9.wireOp",EDGE,"E150");var subQ24=makeQuery(id+"F17.opRevolve","CAP_FACE",FACE,{"disambiguationData":[OSD([subQ23,subQ22,subQ21,subQ20])],"isStart":false});var subQ25=sQuery(id+"F8.wireOp",EDGE,"E125");var subQ26=sQuery(id+"F8.wireOp",EDGE,"E66.MirrorCS");var subQ27=sQuery(id+"F8.wireOp",EDGE,"E43.MirrorCS");var subQ28=makeQuery(id+"F16.opExtrude","CAP_FACE",FACE,{"disambiguationData":[OSD([subQ27,subQ26,sQuery(id+"F8.wireOp",EDGE,"E77"),subQ25])],"isStart":true});var subQ29=sQuery(id+"F8.wireOp",EDGE,"E126");var subQ30=sQuery(id+"F8.wireOp",EDGE,"E65.MirrorCS");var subQ31=sQuery(id+"F8.wireOp",EDGE,"E42.MirrorCS");var subQ32=makeQuery(id+"F16.opExtrude","CAP_FACE",FACE,{"disambiguationData":[OSD([subQ31,subQ30,sQuery(id+"F8.wireOp",EDGE,"E79"),subQ29])],"isStart":true});var subQ33=sQuery(id+"F8.wireOp",EDGE,"E127");var subQ34=sQuery(id+"F8.wireOp",EDGE,"E64.MirrorCS");var subQ35=sQuery(id+"F8.wireOp",EDGE,"E41.MirrorCS");var subQ36=makeQuery(id+"F16.opExtrude","CAP_FACE",FACE,{"disambiguationData":[OSD([subQ35,subQ34,sQuery(id+"F8.wireOp",EDGE,"E81"),subQ33])],"isStart":true});var subQ37=sQuery(id+"F8.wireOp",EDGE,"E128");var subQ38=sQuery(id+"F8.wireOp",EDGE,"E63.MirrorCS");var subQ39=sQuery(id+"F8.wireOp",EDGE,"E40.MirrorCS");var subQ40=makeQuery(id+"F16.opExtrude","CAP_FACE",FACE,{"disambiguationData":[OSD([subQ39,subQ38,sQuery(id+"F8.wireOp",EDGE,"E83"),subQ37])],"isStart":true});var subQ41=sQuery(id+"F8.wireOp",EDGE,"E129");var subQ42=sQuery(id+"F8.wireOp",EDGE,"E51");var subQ43=sQuery(id+"F8.wireOp",EDGE,"E39.MirrorCS");var subQ44=makeQuery(id+"F16.opExtrude","CAP_FACE",FACE,{"disambiguationData":[OSD([subQ43,subQ42,sQuery(id+"F8.wireOp",EDGE,"E85"),subQ41])],"isStart":true});var subQ45=sQuery(id+"F8.wireOp",EDGE,"E141");var subQ46=sQuery(id+"F8.wireOp",EDGE,"E73");var subQ47=sQuery(id+"F8.wireOp",EDGE,"E38.MirrorCS");var subQ48=makeQuery(id+"F16.opExtrude","CAP_FACE",FACE,{"disambiguationData":[OSD([subQ47,subQ46,sQuery(id+"F8.wireOp",EDGE,"E109"),subQ45])],"isStart":true});var subQ49=sQuery(id+"F8.wireOp",EDGE,"E140");var subQ50=sQuery(id+"F8.wireOp",EDGE,"E62.MirrorCS");var subQ51=sQuery(id+"F8.wireOp",EDGE,"E37.MirrorCS");var subQ52=makeQuery(id+"F16.opExtrude","CAP_FACE",FACE,{"disambiguationData":[OSD([subQ51,subQ50,sQuery(id+"F8.wireOp",EDGE,"E107"),subQ49])],"isStart":true});var subQ53=sQuery(id+"F8.wireOp",EDGE,"E139");var subQ54=sQuery(id+"F8.wireOp",EDGE,"E61.MirrorCS");var subQ55=sQuery(id+"F8.wireOp",EDGE,"E36.MirrorCS");var subQ56=makeQuery(id+"F16.opExtrude","CAP_FACE",FACE,{"disambiguationData":[OSD([subQ55,subQ54,sQuery(id+"F8.wireOp",EDGE,"E105"),subQ53])],"isStart":true});var subQ57=sQuery(id+"F8.wireOp",EDGE,"E138");var subQ58=sQuery(id+"F8.wireOp",EDGE,"E60.MirrorCS");var subQ59=sQuery(id+"F8.wireOp",EDGE,"E35.MirrorCS");var subQ60=makeQuery(id+"F16.opExtrude","CAP_FACE",FACE,{"disambiguationData":[OSD([subQ59,subQ58,sQuery(id+"F8.wireOp",EDGE,"E103"),subQ57])],"isStart":true});var subQ61=sQuery(id+"F8.wireOp",EDGE,"E131");var subQ62=sQuery(id+"F8.wireOp",EDGE,"E53");var subQ63=sQuery(id+"F8.wireOp",EDGE,"E28");var subQ64=makeQuery(id+"F16.opExtrude","CAP_FACE",FACE,{"disambiguationData":[OSD([subQ63,subQ62,sQuery(id+"F8.wireOp",EDGE,"E89"),subQ61])],"isStart":true});var subQ65=makeQuery(id+"F17.opRevolve","CAP_FACE",FACE,{"disambiguationData":[OSD([subQ23,subQ22,subQ21,subQ20])],"isStart":true});var subQ66=sQuery(id+"F8.wireOp",EDGE,"E130");var subQ67=sQuery(id+"F8.wireOp",EDGE,"E52");var subQ68=sQuery(id+"F8.wireOp",EDGE,"E27");var subQ69=makeQuery(id+"F16.opExtrude","CAP_FACE",FACE,{"disambiguationData":[OSD([subQ68,subQ67,sQuery(id+"F8.wireOp",EDGE,"E87"),subQ66])],"isStart":true});var subQ70=sQuery(id+"F8.wireOp",EDGE,"E144");var subQ71=sQuery(id+"F8.wireOp",EDGE,"E143");var subQ72=sQuery(id+"F8.wireOp",EDGE,"E142");var subQ73=sQuery(id+"F8.wireOp",EDGE,"E137");var subQ74=sQuery(id+"F8.wireOp",EDGE,"E136");var subQ75=sQuery(id+"F8.wireOp",EDGE,"E135");var subQ76=sQuery(id+"F8.wireOp",EDGE,"E134");var subQ77=sQuery(id+"F8.wireOp",EDGE,"E133");var subQ78=sQuery(id+"F8.wireOp",EDGE,"E132");var subQ79=sQuery(id+"F8.wireOp",EDGE,"E124");var subQ80=sQuery(id+"F8.wireOp",EDGE,"E122");var subQ81=sQuery(id+"F8.wireOp",EDGE,"E119");var subQ82=sQuery(id+"F8.wireOp",EDGE,"E118");var subQ83=sQuery(id+"F8.wireOp",EDGE,"E116");var subQ84=sQuery(id+"F8.wireOp",EDGE,"E114");var subQ85=sQuery(id+"F8.wireOp",EDGE,"E112");var subQ86=sQuery(id+"F8.wireOp",EDGE,"E110");var subQ87=sQuery(id+"F8.wireOp",EDGE,"E108");var subQ88=sQuery(id+"F8.wireOp",EDGE,"E106");var subQ89=sQuery(id+"F8.wireOp",EDGE,"E104");var subQ90=sQuery(id+"F8.wireOp",EDGE,"E102");var subQ91=sQuery(id+"F8.wireOp",EDGE,"E100");var subQ92=sQuery(id+"F8.wireOp",EDGE,"E98");var subQ93=sQuery(id+"F8.wireOp",EDGE,"E96");var subQ94=sQuery(id+"F8.wireOp",EDGE,"E94");var subQ95=sQuery(id+"F8.wireOp",EDGE,"E92");var subQ96=sQuery(id+"F8.wireOp",EDGE,"E90");var subQ97=sQuery(id+"F8.wireOp",EDGE,"E88");var subQ98=sQuery(id+"F8.wireOp",EDGE,"E86");var subQ99=sQuery(id+"F8.wireOp",EDGE,"E84");var subQ100=sQuery(id+"F8.wireOp",EDGE,"E82");var subQ101=sQuery(id+"F8.wireOp",EDGE,"E80");var subQ102=sQuery(id+"F8.wireOp",EDGE,"E78");var subQ103=sQuery(id+"F8.wireOp",EDGE,"E76");var subQ104=sQuery(id+"F8.wireOp",EDGE,"E72.MirrorCS");var subQ105=sQuery(id+"F8.wireOp",EDGE,"E71.MirrorCS");var subQ106=sQuery(id+"F8.wireOp",EDGE,"E70.MirrorCS");var subQ107=sQuery(id+"F8.wireOp",EDGE,"E67.MirrorCS");var subQ108=sQuery(id+"F8.wireOp",EDGE,"E59.MirrorCS");var subQ109=sQuery(id+"F8.wireOp",EDGE,"E58.MirrorCS");var subQ110=sQuery(id+"F8.wireOp",EDGE,"E57");var subQ111=sQuery(id+"F8.wireOp",EDGE,"E56");var subQ112=sQuery(id+"F8.wireOp",EDGE,"E55");var subQ113=sQuery(id+"F8.wireOp",EDGE,"E54");var subQ114=sQuery(id+"F8.wireOp",EDGE,"E50");var subQ115=sQuery(id+"F8.wireOp",EDGE,"E49");var subQ116=sQuery(id+"F8.wireOp",EDGE,"E48.MirrorCS");var subQ117=sQuery(id+"F8.wireOp",EDGE,"E47.MirrorCS");var subQ118=sQuery(id+"F8.wireOp",EDGE,"E34.MirrorCS");var subQ119=sQuery(id+"F8.wireOp",EDGE,"E33");var subQ120=sQuery(id+"F8.wireOp",EDGE,"E32");var subQ121=sQuery(id+"F8.wireOp",EDGE,"E31");var subQ122=sQuery(id+"F8.wireOp",EDGE,"E30");var subQ123=sQuery(id+"F8.wireOp",EDGE,"E29");var subQ124=sQuery(id+"F8.wireOp",EDGE,"E1.0");var subQ125=makeQuery(id+"F15.opExtrude","CAP_FACE",FACE,{"disambiguationData":[OSD([subQ124,subQ68,subQ63,subQ123,subQ122,subQ121,subQ120,subQ119,subQ118,subQ59,subQ55,subQ51,subQ47,subQ43,subQ39,subQ35,subQ31,subQ27,subQ18,subQ13,subQ2,subQ117,subQ116,subQ115,subQ114,subQ42,subQ67,subQ62,subQ113,subQ112,subQ111,subQ110,subQ109,subQ108,subQ58,subQ54,subQ50,subQ38,subQ34,subQ30,subQ26,subQ107,subQ12,subQ1,subQ106,subQ105,subQ104,subQ46,subQ17,subQ103,subQ102,subQ101,subQ100,subQ99,subQ98,subQ97,subQ96,subQ95,subQ94,subQ93,subQ92,subQ91,subQ90,subQ89,subQ88,subQ87,subQ86,subQ85,subQ84,subQ83,subQ82,subQ81,subQ80,subQ79,subQ25,subQ29,subQ33,subQ37,subQ41,subQ66,subQ61,subQ78,subQ77,subQ76,subQ75,subQ74,subQ73,subQ57,subQ53,subQ49,subQ45,subQ72,subQ71,subQ70,subQ0,subQ11,subQ16])],"isStart":true});var subQ126=makeQuery(id+"F16.opExtrude","CAP_FACE",FACE,{"disambiguationData":[OSD([subQ114,subQ107,sQuery(id+"F8.wireOp",EDGE,"E123"),subQ79])],"isStart":true});var subQ127=makeQuery(id+"F16.opExtrude","CAP_FACE",FACE,{"disambiguationData":[OSD([subQ119,subQ109,sQuery(id+"F8.wireOp",EDGE,"E99"),subQ74])],"isStart":true});var subQ129=makeQuery(id+"F16.opExtrude","CAP_FACE",FACE,{"disambiguationData":[OSD([subQ123,subQ113,sQuery(id+"F8.wireOp",EDGE,"E91"),subQ78])],"isStart":true});var subQ130=makeQuery(id+"F16.opExtrude","CAP_FACE",FACE,{"disambiguationData":[OSD([subQ122,subQ112,sQuery(id+"F8.wireOp",EDGE,"E93"),subQ77])],"isStart":true});var subQ131=makeQuery(id+"F19.opExtrude","CAP_FACE",FACE,{"disambiguationData":[OSD([subQ9,subQ8,subQ7,subQ6,subQ5,subQ4])],"isStart":true});var subQ132=makeQuery(id+"F16.opExtrude","CAP_FACE",FACE,{"disambiguationData":[OSD([subQ121,subQ111,sQuery(id+"F8.wireOp",EDGE,"E95"),subQ76])],"isStart":true});var subQ133=makeQuery(id+"F19.opExtrude","SWEPT_FACE",FACE,{"disambiguationData":[OSD([subQ7])]});var subQ139=makeQuery(id+"F15.opExtrude","CAP_FACE",FACE,{"disambiguationData":[OSD([subQ124,subQ68,subQ63,subQ123,subQ122,subQ121,subQ120,subQ119,subQ118,subQ59,subQ55,subQ51,subQ47,subQ43,subQ39,subQ35,subQ31,subQ27,subQ18,subQ13,subQ2,subQ117,subQ116,subQ115,subQ114,subQ42,subQ67,subQ62,subQ113,subQ112,subQ111,subQ110,subQ109,subQ108,subQ58,subQ54,subQ50,subQ38,subQ34,subQ30,subQ26,subQ107,subQ12,subQ1,subQ106,subQ105,subQ104,subQ46,subQ17,subQ103,subQ102,subQ101,subQ100,subQ99,subQ98,subQ97,subQ96,subQ95,subQ94,subQ93,subQ92,subQ91,subQ90,subQ89,subQ88,subQ87,subQ86,subQ85,subQ84,subQ83,subQ82,subQ81,subQ80,subQ79,subQ25,subQ29,subQ33,subQ37,subQ41,subQ66,subQ61,subQ78,subQ77,subQ76,subQ75,subQ74,subQ73,subQ57,subQ53,subQ49,subQ45,subQ72,subQ71,subQ70,subQ0,subQ11,subQ16])],"isStart":false});var subQ140=makeQuery(id+"F16.opExtrude","CAP_FACE",FACE,{"disambiguationData":[OSD([subQ120,subQ110,sQuery(id+"F8.wireOp",EDGE,"E97"),subQ75])],"isStart":true});var subQ141=makeQuery(id+"F19.opExtrude","SWEPT_FACE",FACE,{"disambiguationData":[OSD([subQ4])]});var subQ142=makeQuery(id+"F16.opExtrude","CAP_FACE",FACE,{"disambiguationData":[OSD([subQ118,subQ108,sQuery(id+"F8.wireOp",EDGE,"E101"),subQ73])],"isStart":true});var subQ143=makeQuery(id+"F16.opExtrude","CAP_FACE",FACE,{"disambiguationData":[OSD([subQ117,subQ106,sQuery(id+"F8.wireOp",EDGE,"E115"),subQ70])],"isStart":true});var subQ144=makeQuery(id+"F16.opExtrude","CAP_FACE",FACE,{"disambiguationData":[OSD([subQ116,subQ105,sQuery(id+"F8.wireOp",EDGE,"E113"),subQ71])],"isStart":true});var subQ145=makeQuery(id+"F16.opExtrude","CAP_FACE",FACE,{"disambiguationData":[OSD([subQ115,subQ104,sQuery(id+"F8.wireOp",EDGE,"E111"),subQ72])],"isStart":true});var subQ146=makeQuery(id+"F18.opRevolve","SWEPT_FACE",FACE,{"disambiguationData":[OSD([subQ20])]});var subQ147=makeQuery(id+"F19.opExtrude","SWEPT_FACE",FACE,{"disambiguationData":[OSD([subQ8])]});var subQ148=makeQuery(id+"F19.opExtrude","SWEPT_FACE",FACE,{"disambiguationData":[OSD([subQ5])]});Q0=makeQuery(id+"F21.boolean.opBoolean","INTERSECT",EDGE,{"derivedFrom":[makeQuery(id+"F20.boolean.opBoolean","SPLIT",FACE,{"disambiguationData":[TD([subQ15])],"derivedFrom":makeQuery(id+"F19.boolean.opBoolean","SPLIT",FACE,{"disambiguationData":[TD([makeQuery(id+"F15.opExtrude","SWEPT_FACE",FACE,{"disambiguationData":[OSD([subQ124])]}),subQ125,subQ139,subQ69,subQ64,subQ129,subQ130,subQ132,subQ140,subQ127,subQ142,subQ60,subQ56,subQ52,subQ48,subQ44,subQ40,subQ36,subQ32,subQ28,subQ19,subQ14,subQ3,subQ143,subQ144,subQ145,subQ126,subQ65,subQ24,subQ15,subQ146,subQ131,subQ10,subQ147,subQ133,subQ148,subQ141])],"derivedFrom":makeQuery(id+"F18.boolean.opBoolean","MERGE",FACE,{"derivedFrom":[makeQuery(id+"F17.opRevolve","SWEPT_FACE",FACE,{"disambiguationData":[OSD([subQ23])]}),makeQuery(id+"F18.opRevolve","SWEPT_FACE",FACE,{"disambiguationData":[OSD([subQ23])]})]})})}),makeQuery(id+"F21.opExtrude","SWEPT_FACE",FACE,{"disambiguationData":[OSD([sQuery(id+"F13.wireOp",EDGE,"E296.MirrorCS")])]})]});}
            var Q1;
            {var subQ0=sQuery(id+"F8.wireOp",EDGE,"E145");var subQ1=sQuery(id+"F8.wireOp",EDGE,"E69.MirrorCS");var subQ2=sQuery(id+"F8.wireOp",EDGE,"E46.MirrorCS");var subQ3=makeQuery(id+"F16.opExtrude","CAP_FACE",FACE,{"disambiguationData":[OSD([subQ2,subQ1,sQuery(id+"F8.wireOp",EDGE,"E117"),subQ0])],"isStart":true});var subQ4=sQuery(id+"F12.wireOp",EDGE,"E290");var subQ5=sQuery(id+"F12.wireOp",EDGE,"E289");var subQ6=sQuery(id+"F12.wireOp",EDGE,"E288");var subQ7=sQuery(id+"F12.wireOp",EDGE,"E287");var subQ8=sQuery(id+"F12.wireOp",EDGE,"E286");var subQ9=sQuery(id+"F12.wireOp",EDGE,"E285");var subQ10=makeQuery(id+"F19.opExtrude","CAP_FACE",FACE,{"disambiguationData":[OSD([subQ9,subQ8,subQ7,subQ6,subQ5,subQ4])],"isStart":false});var subQ11=sQuery(id+"F8.wireOp",EDGE,"E146");var subQ12=sQuery(id+"F8.wireOp",EDGE,"E68.MirrorCS");var subQ13=sQuery(id+"F8.wireOp",EDGE,"E45.MirrorCS");var subQ14=makeQuery(id+"F16.opExtrude","CAP_FACE",FACE,{"disambiguationData":[OSD([subQ13,subQ12,sQuery(id+"F8.wireOp",EDGE,"E120"),subQ11])],"isStart":true});var subQ15=makeQuery(id+"F18.opRevolve","SWEPT_FACE",FACE,{"disambiguationData":[OSD([sQuery(id+"F9.wireOp",EDGE,"E157")])]});var subQ16=sQuery(id+"F8.wireOp",EDGE,"E147");var subQ17=sQuery(id+"F8.wireOp",EDGE,"E74");var subQ18=sQuery(id+"F8.wireOp",EDGE,"E44.MirrorCS");var subQ19=makeQuery(id+"F16.opExtrude","CAP_FACE",FACE,{"disambiguationData":[OSD([subQ18,subQ17,sQuery(id+"F8.wireOp",EDGE,"E121"),subQ16])],"isStart":true});var subQ20=sQuery(id+"F9.wireOp",EDGE,"E164");var subQ21=sQuery(id+"F9.wireOp",EDGE,"E152");var subQ22=sQuery(id+"F9.wireOp",EDGE,"E151");var subQ23=sQuery(id+"F9.wireOp",EDGE,"E150");var subQ24=makeQuery(id+"F17.opRevolve","CAP_FACE",FACE,{"disambiguationData":[OSD([subQ23,subQ22,subQ21,subQ20])],"isStart":false});var subQ25=sQuery(id+"F8.wireOp",EDGE,"E125");var subQ26=sQuery(id+"F8.wireOp",EDGE,"E66.MirrorCS");var subQ27=sQuery(id+"F8.wireOp",EDGE,"E43.MirrorCS");var subQ28=makeQuery(id+"F16.opExtrude","CAP_FACE",FACE,{"disambiguationData":[OSD([subQ27,subQ26,sQuery(id+"F8.wireOp",EDGE,"E77"),subQ25])],"isStart":true});var subQ29=sQuery(id+"F8.wireOp",EDGE,"E126");var subQ30=sQuery(id+"F8.wireOp",EDGE,"E65.MirrorCS");var subQ31=sQuery(id+"F8.wireOp",EDGE,"E42.MirrorCS");var subQ32=makeQuery(id+"F16.opExtrude","CAP_FACE",FACE,{"disambiguationData":[OSD([subQ31,subQ30,sQuery(id+"F8.wireOp",EDGE,"E79"),subQ29])],"isStart":true});var subQ33=sQuery(id+"F8.wireOp",EDGE,"E127");var subQ34=sQuery(id+"F8.wireOp",EDGE,"E64.MirrorCS");var subQ35=sQuery(id+"F8.wireOp",EDGE,"E41.MirrorCS");var subQ36=makeQuery(id+"F16.opExtrude","CAP_FACE",FACE,{"disambiguationData":[OSD([subQ35,subQ34,sQuery(id+"F8.wireOp",EDGE,"E81"),subQ33])],"isStart":true});var subQ37=sQuery(id+"F8.wireOp",EDGE,"E128");var subQ38=sQuery(id+"F8.wireOp",EDGE,"E63.MirrorCS");var subQ39=sQuery(id+"F8.wireOp",EDGE,"E40.MirrorCS");var subQ40=makeQuery(id+"F16.opExtrude","CAP_FACE",FACE,{"disambiguationData":[OSD([subQ39,subQ38,sQuery(id+"F8.wireOp",EDGE,"E83"),subQ37])],"isStart":true});var subQ41=sQuery(id+"F8.wireOp",EDGE,"E129");var subQ42=sQuery(id+"F8.wireOp",EDGE,"E51");var subQ43=sQuery(id+"F8.wireOp",EDGE,"E39.MirrorCS");var subQ44=makeQuery(id+"F16.opExtrude","CAP_FACE",FACE,{"disambiguationData":[OSD([subQ43,subQ42,sQuery(id+"F8.wireOp",EDGE,"E85"),subQ41])],"isStart":true});var subQ45=sQuery(id+"F8.wireOp",EDGE,"E141");var subQ46=sQuery(id+"F8.wireOp",EDGE,"E73");var subQ47=sQuery(id+"F8.wireOp",EDGE,"E38.MirrorCS");var subQ48=makeQuery(id+"F16.opExtrude","CAP_FACE",FACE,{"disambiguationData":[OSD([subQ47,subQ46,sQuery(id+"F8.wireOp",EDGE,"E109"),subQ45])],"isStart":true});var subQ49=sQuery(id+"F8.wireOp",EDGE,"E140");var subQ50=sQuery(id+"F8.wireOp",EDGE,"E62.MirrorCS");var subQ51=sQuery(id+"F8.wireOp",EDGE,"E37.MirrorCS");var subQ52=makeQuery(id+"F16.opExtrude","CAP_FACE",FACE,{"disambiguationData":[OSD([subQ51,subQ50,sQuery(id+"F8.wireOp",EDGE,"E107"),subQ49])],"isStart":true});var subQ53=sQuery(id+"F8.wireOp",EDGE,"E139");var subQ54=sQuery(id+"F8.wireOp",EDGE,"E61.MirrorCS");var subQ55=sQuery(id+"F8.wireOp",EDGE,"E36.MirrorCS");var subQ56=makeQuery(id+"F16.opExtrude","CAP_FACE",FACE,{"disambiguationData":[OSD([subQ55,subQ54,sQuery(id+"F8.wireOp",EDGE,"E105"),subQ53])],"isStart":true});var subQ57=sQuery(id+"F8.wireOp",EDGE,"E138");var subQ58=sQuery(id+"F8.wireOp",EDGE,"E60.MirrorCS");var subQ59=sQuery(id+"F8.wireOp",EDGE,"E35.MirrorCS");var subQ60=makeQuery(id+"F16.opExtrude","CAP_FACE",FACE,{"disambiguationData":[OSD([subQ59,subQ58,sQuery(id+"F8.wireOp",EDGE,"E103"),subQ57])],"isStart":true});var subQ61=sQuery(id+"F8.wireOp",EDGE,"E131");var subQ62=sQuery(id+"F8.wireOp",EDGE,"E53");var subQ63=sQuery(id+"F8.wireOp",EDGE,"E28");var subQ64=makeQuery(id+"F16.opExtrude","CAP_FACE",FACE,{"disambiguationData":[OSD([subQ63,subQ62,sQuery(id+"F8.wireOp",EDGE,"E89"),subQ61])],"isStart":true});var subQ65=makeQuery(id+"F17.opRevolve","CAP_FACE",FACE,{"disambiguationData":[OSD([subQ23,subQ22,subQ21,subQ20])],"isStart":true});var subQ66=sQuery(id+"F8.wireOp",EDGE,"E130");var subQ67=sQuery(id+"F8.wireOp",EDGE,"E52");var subQ68=sQuery(id+"F8.wireOp",EDGE,"E27");var subQ69=makeQuery(id+"F16.opExtrude","CAP_FACE",FACE,{"disambiguationData":[OSD([subQ68,subQ67,sQuery(id+"F8.wireOp",EDGE,"E87"),subQ66])],"isStart":true});var subQ70=sQuery(id+"F8.wireOp",EDGE,"E144");var subQ71=sQuery(id+"F8.wireOp",EDGE,"E143");var subQ72=sQuery(id+"F8.wireOp",EDGE,"E142");var subQ73=sQuery(id+"F8.wireOp",EDGE,"E137");var subQ74=sQuery(id+"F8.wireOp",EDGE,"E136");var subQ75=sQuery(id+"F8.wireOp",EDGE,"E135");var subQ76=sQuery(id+"F8.wireOp",EDGE,"E134");var subQ77=sQuery(id+"F8.wireOp",EDGE,"E133");var subQ78=sQuery(id+"F8.wireOp",EDGE,"E132");var subQ79=sQuery(id+"F8.wireOp",EDGE,"E124");var subQ80=sQuery(id+"F8.wireOp",EDGE,"E122");var subQ81=sQuery(id+"F8.wireOp",EDGE,"E119");var subQ82=sQuery(id+"F8.wireOp",EDGE,"E118");var subQ83=sQuery(id+"F8.wireOp",EDGE,"E116");var subQ84=sQuery(id+"F8.wireOp",EDGE,"E114");var subQ85=sQuery(id+"F8.wireOp",EDGE,"E112");var subQ86=sQuery(id+"F8.wireOp",EDGE,"E110");var subQ87=sQuery(id+"F8.wireOp",EDGE,"E108");var subQ88=sQuery(id+"F8.wireOp",EDGE,"E106");var subQ89=sQuery(id+"F8.wireOp",EDGE,"E104");var subQ90=sQuery(id+"F8.wireOp",EDGE,"E102");var subQ91=sQuery(id+"F8.wireOp",EDGE,"E100");var subQ92=sQuery(id+"F8.wireOp",EDGE,"E98");var subQ93=sQuery(id+"F8.wireOp",EDGE,"E96");var subQ94=sQuery(id+"F8.wireOp",EDGE,"E94");var subQ95=sQuery(id+"F8.wireOp",EDGE,"E92");var subQ96=sQuery(id+"F8.wireOp",EDGE,"E90");var subQ97=sQuery(id+"F8.wireOp",EDGE,"E88");var subQ98=sQuery(id+"F8.wireOp",EDGE,"E86");var subQ99=sQuery(id+"F8.wireOp",EDGE,"E84");var subQ100=sQuery(id+"F8.wireOp",EDGE,"E82");var subQ101=sQuery(id+"F8.wireOp",EDGE,"E80");var subQ102=sQuery(id+"F8.wireOp",EDGE,"E78");var subQ103=sQuery(id+"F8.wireOp",EDGE,"E76");var subQ104=sQuery(id+"F8.wireOp",EDGE,"E72.MirrorCS");var subQ105=sQuery(id+"F8.wireOp",EDGE,"E71.MirrorCS");var subQ106=sQuery(id+"F8.wireOp",EDGE,"E70.MirrorCS");var subQ107=sQuery(id+"F8.wireOp",EDGE,"E67.MirrorCS");var subQ108=sQuery(id+"F8.wireOp",EDGE,"E59.MirrorCS");var subQ109=sQuery(id+"F8.wireOp",EDGE,"E58.MirrorCS");var subQ110=sQuery(id+"F8.wireOp",EDGE,"E57");var subQ111=sQuery(id+"F8.wireOp",EDGE,"E56");var subQ112=sQuery(id+"F8.wireOp",EDGE,"E55");var subQ113=sQuery(id+"F8.wireOp",EDGE,"E54");var subQ114=sQuery(id+"F8.wireOp",EDGE,"E50");var subQ115=sQuery(id+"F8.wireOp",EDGE,"E49");var subQ116=sQuery(id+"F8.wireOp",EDGE,"E48.MirrorCS");var subQ117=sQuery(id+"F8.wireOp",EDGE,"E47.MirrorCS");var subQ118=sQuery(id+"F8.wireOp",EDGE,"E34.MirrorCS");var subQ119=sQuery(id+"F8.wireOp",EDGE,"E33");var subQ120=sQuery(id+"F8.wireOp",EDGE,"E32");var subQ121=sQuery(id+"F8.wireOp",EDGE,"E31");var subQ122=sQuery(id+"F8.wireOp",EDGE,"E30");var subQ123=sQuery(id+"F8.wireOp",EDGE,"E29");var subQ124=sQuery(id+"F8.wireOp",EDGE,"E1.0");var subQ125=makeQuery(id+"F15.opExtrude","CAP_FACE",FACE,{"disambiguationData":[OSD([subQ124,subQ68,subQ63,subQ123,subQ122,subQ121,subQ120,subQ119,subQ118,subQ59,subQ55,subQ51,subQ47,subQ43,subQ39,subQ35,subQ31,subQ27,subQ18,subQ13,subQ2,subQ117,subQ116,subQ115,subQ114,subQ42,subQ67,subQ62,subQ113,subQ112,subQ111,subQ110,subQ109,subQ108,subQ58,subQ54,subQ50,subQ38,subQ34,subQ30,subQ26,subQ107,subQ12,subQ1,subQ106,subQ105,subQ104,subQ46,subQ17,subQ103,subQ102,subQ101,subQ100,subQ99,subQ98,subQ97,subQ96,subQ95,subQ94,subQ93,subQ92,subQ91,subQ90,subQ89,subQ88,subQ87,subQ86,subQ85,subQ84,subQ83,subQ82,subQ81,subQ80,subQ79,subQ25,subQ29,subQ33,subQ37,subQ41,subQ66,subQ61,subQ78,subQ77,subQ76,subQ75,subQ74,subQ73,subQ57,subQ53,subQ49,subQ45,subQ72,subQ71,subQ70,subQ0,subQ11,subQ16])],"isStart":true});var subQ126=makeQuery(id+"F16.opExtrude","CAP_FACE",FACE,{"disambiguationData":[OSD([subQ114,subQ107,sQuery(id+"F8.wireOp",EDGE,"E123"),subQ79])],"isStart":true});var subQ127=makeQuery(id+"F16.opExtrude","CAP_FACE",FACE,{"disambiguationData":[OSD([subQ119,subQ109,sQuery(id+"F8.wireOp",EDGE,"E99"),subQ74])],"isStart":true});var subQ129=makeQuery(id+"F16.opExtrude","CAP_FACE",FACE,{"disambiguationData":[OSD([subQ123,subQ113,sQuery(id+"F8.wireOp",EDGE,"E91"),subQ78])],"isStart":true});var subQ130=makeQuery(id+"F16.opExtrude","CAP_FACE",FACE,{"disambiguationData":[OSD([subQ122,subQ112,sQuery(id+"F8.wireOp",EDGE,"E93"),subQ77])],"isStart":true});var subQ131=makeQuery(id+"F19.opExtrude","CAP_FACE",FACE,{"disambiguationData":[OSD([subQ9,subQ8,subQ7,subQ6,subQ5,subQ4])],"isStart":true});var subQ132=makeQuery(id+"F16.opExtrude","CAP_FACE",FACE,{"disambiguationData":[OSD([subQ121,subQ111,sQuery(id+"F8.wireOp",EDGE,"E95"),subQ76])],"isStart":true});var subQ133=makeQuery(id+"F19.opExtrude","SWEPT_FACE",FACE,{"disambiguationData":[OSD([subQ7])]});var subQ139=makeQuery(id+"F15.opExtrude","CAP_FACE",FACE,{"disambiguationData":[OSD([subQ124,subQ68,subQ63,subQ123,subQ122,subQ121,subQ120,subQ119,subQ118,subQ59,subQ55,subQ51,subQ47,subQ43,subQ39,subQ35,subQ31,subQ27,subQ18,subQ13,subQ2,subQ117,subQ116,subQ115,subQ114,subQ42,subQ67,subQ62,subQ113,subQ112,subQ111,subQ110,subQ109,subQ108,subQ58,subQ54,subQ50,subQ38,subQ34,subQ30,subQ26,subQ107,subQ12,subQ1,subQ106,subQ105,subQ104,subQ46,subQ17,subQ103,subQ102,subQ101,subQ100,subQ99,subQ98,subQ97,subQ96,subQ95,subQ94,subQ93,subQ92,subQ91,subQ90,subQ89,subQ88,subQ87,subQ86,subQ85,subQ84,subQ83,subQ82,subQ81,subQ80,subQ79,subQ25,subQ29,subQ33,subQ37,subQ41,subQ66,subQ61,subQ78,subQ77,subQ76,subQ75,subQ74,subQ73,subQ57,subQ53,subQ49,subQ45,subQ72,subQ71,subQ70,subQ0,subQ11,subQ16])],"isStart":false});var subQ140=makeQuery(id+"F16.opExtrude","CAP_FACE",FACE,{"disambiguationData":[OSD([subQ120,subQ110,sQuery(id+"F8.wireOp",EDGE,"E97"),subQ75])],"isStart":true});var subQ141=makeQuery(id+"F19.opExtrude","SWEPT_FACE",FACE,{"disambiguationData":[OSD([subQ4])]});var subQ142=makeQuery(id+"F16.opExtrude","CAP_FACE",FACE,{"disambiguationData":[OSD([subQ118,subQ108,sQuery(id+"F8.wireOp",EDGE,"E101"),subQ73])],"isStart":true});var subQ143=makeQuery(id+"F16.opExtrude","CAP_FACE",FACE,{"disambiguationData":[OSD([subQ117,subQ106,sQuery(id+"F8.wireOp",EDGE,"E115"),subQ70])],"isStart":true});var subQ144=makeQuery(id+"F16.opExtrude","CAP_FACE",FACE,{"disambiguationData":[OSD([subQ116,subQ105,sQuery(id+"F8.wireOp",EDGE,"E113"),subQ71])],"isStart":true});var subQ145=makeQuery(id+"F16.opExtrude","CAP_FACE",FACE,{"disambiguationData":[OSD([subQ115,subQ104,sQuery(id+"F8.wireOp",EDGE,"E111"),subQ72])],"isStart":true});var subQ146=makeQuery(id+"F18.opRevolve","SWEPT_FACE",FACE,{"disambiguationData":[OSD([subQ20])]});var subQ147=makeQuery(id+"F19.opExtrude","SWEPT_FACE",FACE,{"disambiguationData":[OSD([subQ8])]});var subQ148=makeQuery(id+"F19.opExtrude","SWEPT_FACE",FACE,{"disambiguationData":[OSD([subQ5])]});Q1=makeQuery(id+"F21.boolean.opBoolean","INTERSECT",EDGE,{"derivedFrom":[makeQuery(id+"F20.boolean.opBoolean","SPLIT",FACE,{"disambiguationData":[TD([subQ15])],"derivedFrom":makeQuery(id+"F19.boolean.opBoolean","SPLIT",FACE,{"disambiguationData":[TD([makeQuery(id+"F15.opExtrude","SWEPT_FACE",FACE,{"disambiguationData":[OSD([subQ124])]}),subQ125,subQ139,subQ69,subQ64,subQ129,subQ130,subQ132,subQ140,subQ127,subQ142,subQ60,subQ56,subQ52,subQ48,subQ44,subQ40,subQ36,subQ32,subQ28,subQ19,subQ14,subQ3,subQ143,subQ144,subQ145,subQ126,subQ65,subQ24,subQ15,subQ146,subQ131,subQ10,subQ147,subQ133,subQ148,subQ141])],"derivedFrom":makeQuery(id+"F18.boolean.opBoolean","MERGE",FACE,{"derivedFrom":[makeQuery(id+"F17.opRevolve","SWEPT_FACE",FACE,{"disambiguationData":[OSD([subQ23])]}),makeQuery(id+"F18.opRevolve","SWEPT_FACE",FACE,{"disambiguationData":[OSD([subQ23])]})]})})}),makeQuery(id+"F21.opExtrude","SWEPT_FACE",FACE,{"disambiguationData":[OSD([sQuery(id+"F13.wireOp",EDGE,"E295.MirrorCS")])]})]});}
            fillet(context, id + "F38", {"entities" : qUnion([Q0, Q1]), "radius" : 5 * mm, "tangentPropagation" : true, "allowEdgeOverflow" : false});
        }
        {
            var Q0;
            Q0=makeQuery(id+"F24.boolean.opBoolean","MERGE",EDGE,{"derivedFrom":[makeQuery(id+"F23.opExtrude","SWEPT_EDGE",EDGE,{"disambiguationData":[OSD([sQuery(id+"F13.wireOp",EDGE,"E307"),sQuery(id+"F13.wireOp",EDGE,"E308")])]}),makeQuery(id+"F24.opExtrude","SWEPT_EDGE",EDGE,{"disambiguationData":[OSD([sQuery(id+"F14.wireOp",EDGE,"E325"),sQuery(id+"F14.wireOp",EDGE,"E326")])]})]});
            var Q1;
            Q1=makeQuery(id+"F24.boolean.opBoolean","MERGE",EDGE,{"derivedFrom":[makeQuery(id+"F23.opExtrude","SWEPT_EDGE",EDGE,{"disambiguationData":[OSD([sQuery(id+"F13.wireOp",EDGE,"E308"),sQuery(id+"F13.wireOp",EDGE,"E309")])]}),makeQuery(id+"F24.opExtrude","SWEPT_EDGE",EDGE,{"disambiguationData":[OSD([sQuery(id+"F14.wireOp",EDGE,"E326"),sQuery(id+"F14.wireOp",EDGE,"E327")])]})]});
            var Q2;
            Q2=makeQuery(id+"F24.opExtrude","SWEPT_EDGE",EDGE,{"disambiguationData":[OSD([sQuery(id+"F14.wireOp",EDGE,"E314.MirrorCS"),sQuery(id+"F14.wireOp",EDGE,"E329.0")])]});
            var Q3;
            Q3=makeQuery(id+"F24.opExtrude","SWEPT_EDGE",EDGE,{"disambiguationData":[OSD([sQuery(id+"F14.wireOp",EDGE,"E313.MirrorCS"),sQuery(id+"F14.wireOp",EDGE,"E329.0")])]});
            var Q4;
            Q4=makeQuery(id+"F23.opExtrude","CAP_EDGE",EDGE,{"disambiguationData":[OSD([sQuery(id+"F13.wireOp",EDGE,"E308")])],"isStart":true});
            var Q5;
            Q5=makeQuery(id+"F23.opExtrude","CAP_EDGE",EDGE,{"disambiguationData":[OSD([sQuery(id+"F13.wireOp",EDGE,"E309")])],"isStart":true});
            var Q6;
            Q6=makeQuery(id+"F23.opExtrude","CAP_EDGE",EDGE,{"disambiguationData":[OSD([sQuery(id+"F13.wireOp",EDGE,"E307")])],"isStart":true});
            var Q7;
            {var subQ3=sQuery(id+"F11.wireOp",EDGE,"E261");var subQ4=sQuery(id+"F11.wireOp",EDGE,"E260");var subQ8=sQuery(id+"F9.wireOp",EDGE,"E150");var subQ9=makeQuery(id+"F18.opRevolve","SWEPT_FACE",FACE,{"disambiguationData":[OSD([subQ8])]});var subQ10=makeQuery(id+"F17.opRevolve","SWEPT_FACE",FACE,{"disambiguationData":[OSD([subQ8])]});var subQ11=makeQuery(id+"F20.opExtrude","SWEPT_FACE",FACE,{"disambiguationData":[OSD([subQ4])]});var subQ12=makeQuery(id+"F21.opExtrude","SWEPT_FACE",FACE,{"disambiguationData":[OSD([sQuery(id+"F13.wireOp",EDGE,"E296.MirrorCS")])]});var subQ13=sQuery(id+"F13.wireOp",EDGE,"E309");var subQ14=makeQuery(id+"F20.opExtrude","SWEPT_FACE",FACE,{"disambiguationData":[OSD([subQ3])]});var subQ15=sQuery(id+"F12.wireOp",EDGE,"E287");var subQ16=makeQuery(id+"F19.opExtrude","SWEPT_FACE",FACE,{"disambiguationData":[OSD([subQ15])]});var subQ17=sQuery(id+"F8.wireOp",EDGE,"E145");var subQ18=sQuery(id+"F8.wireOp",EDGE,"E69.MirrorCS");var subQ19=sQuery(id+"F8.wireOp",EDGE,"E46.MirrorCS");var subQ20=makeQuery(id+"F16.opExtrude","CAP_FACE",FACE,{"disambiguationData":[OSD([subQ19,subQ18,sQuery(id+"F8.wireOp",EDGE,"E117"),subQ17])],"isStart":true});var subQ21=sQuery(id+"F12.wireOp",EDGE,"E290");var subQ22=sQuery(id+"F12.wireOp",EDGE,"E289");var subQ23=sQuery(id+"F12.wireOp",EDGE,"E288");var subQ24=sQuery(id+"F12.wireOp",EDGE,"E286");var subQ25=sQuery(id+"F12.wireOp",EDGE,"E285");var subQ26=makeQuery(id+"F19.opExtrude","CAP_FACE",FACE,{"disambiguationData":[OSD([subQ25,subQ24,subQ15,subQ23,subQ22,subQ21])],"isStart":false});var subQ27=sQuery(id+"F8.wireOp",EDGE,"E146");var subQ28=sQuery(id+"F8.wireOp",EDGE,"E68.MirrorCS");var subQ29=sQuery(id+"F8.wireOp",EDGE,"E45.MirrorCS");var subQ30=makeQuery(id+"F16.opExtrude","CAP_FACE",FACE,{"disambiguationData":[OSD([subQ29,subQ28,sQuery(id+"F8.wireOp",EDGE,"E120"),subQ27])],"isStart":true});var subQ31=makeQuery(id+"F18.opRevolve","SWEPT_FACE",FACE,{"disambiguationData":[OSD([sQuery(id+"F9.wireOp",EDGE,"E157")])]});var subQ32=sQuery(id+"F8.wireOp",EDGE,"E147");var subQ33=sQuery(id+"F8.wireOp",EDGE,"E74");var subQ34=sQuery(id+"F8.wireOp",EDGE,"E44.MirrorCS");var subQ35=makeQuery(id+"F16.opExtrude","CAP_FACE",FACE,{"disambiguationData":[OSD([subQ34,subQ33,sQuery(id+"F8.wireOp",EDGE,"E121"),subQ32])],"isStart":true});var subQ36=sQuery(id+"F9.wireOp",EDGE,"E164");var subQ37=sQuery(id+"F9.wireOp",EDGE,"E152");var subQ38=sQuery(id+"F9.wireOp",EDGE,"E151");var subQ39=makeQuery(id+"F17.opRevolve","CAP_FACE",FACE,{"disambiguationData":[OSD([subQ8,subQ38,subQ37,subQ36])],"isStart":false});var subQ40=sQuery(id+"F8.wireOp",EDGE,"E125");var subQ41=sQuery(id+"F8.wireOp",EDGE,"E66.MirrorCS");var subQ42=sQuery(id+"F8.wireOp",EDGE,"E43.MirrorCS");var subQ43=makeQuery(id+"F16.opExtrude","CAP_FACE",FACE,{"disambiguationData":[OSD([subQ42,subQ41,sQuery(id+"F8.wireOp",EDGE,"E77"),subQ40])],"isStart":true});var subQ44=sQuery(id+"F8.wireOp",EDGE,"E126");var subQ45=sQuery(id+"F8.wireOp",EDGE,"E65.MirrorCS");var subQ46=sQuery(id+"F8.wireOp",EDGE,"E42.MirrorCS");var subQ47=makeQuery(id+"F16.opExtrude","CAP_FACE",FACE,{"disambiguationData":[OSD([subQ46,subQ45,sQuery(id+"F8.wireOp",EDGE,"E79"),subQ44])],"isStart":true});var subQ48=sQuery(id+"F8.wireOp",EDGE,"E127");var subQ49=sQuery(id+"F8.wireOp",EDGE,"E64.MirrorCS");var subQ50=sQuery(id+"F8.wireOp",EDGE,"E41.MirrorCS");var subQ51=makeQuery(id+"F16.opExtrude","CAP_FACE",FACE,{"disambiguationData":[OSD([subQ50,subQ49,sQuery(id+"F8.wireOp",EDGE,"E81"),subQ48])],"isStart":true});var subQ52=sQuery(id+"F8.wireOp",EDGE,"E128");var subQ53=sQuery(id+"F8.wireOp",EDGE,"E63.MirrorCS");var subQ54=sQuery(id+"F8.wireOp",EDGE,"E40.MirrorCS");var subQ55=makeQuery(id+"F16.opExtrude","CAP_FACE",FACE,{"disambiguationData":[OSD([subQ54,subQ53,sQuery(id+"F8.wireOp",EDGE,"E83"),subQ52])],"isStart":true});var subQ56=sQuery(id+"F8.wireOp",EDGE,"E129");var subQ57=sQuery(id+"F8.wireOp",EDGE,"E51");var subQ58=sQuery(id+"F8.wireOp",EDGE,"E39.MirrorCS");var subQ59=makeQuery(id+"F16.opExtrude","CAP_FACE",FACE,{"disambiguationData":[OSD([subQ58,subQ57,sQuery(id+"F8.wireOp",EDGE,"E85"),subQ56])],"isStart":true});var subQ60=sQuery(id+"F8.wireOp",EDGE,"E141");var subQ61=sQuery(id+"F8.wireOp",EDGE,"E73");var subQ62=sQuery(id+"F8.wireOp",EDGE,"E38.MirrorCS");var subQ63=makeQuery(id+"F16.opExtrude","CAP_FACE",FACE,{"disambiguationData":[OSD([subQ62,subQ61,sQuery(id+"F8.wireOp",EDGE,"E109"),subQ60])],"isStart":true});var subQ64=sQuery(id+"F8.wireOp",EDGE,"E140");var subQ65=sQuery(id+"F8.wireOp",EDGE,"E62.MirrorCS");var subQ66=sQuery(id+"F8.wireOp",EDGE,"E37.MirrorCS");var subQ67=makeQuery(id+"F16.opExtrude","CAP_FACE",FACE,{"disambiguationData":[OSD([subQ66,subQ65,sQuery(id+"F8.wireOp",EDGE,"E107"),subQ64])],"isStart":true});var subQ68=sQuery(id+"F8.wireOp",EDGE,"E139");var subQ69=sQuery(id+"F8.wireOp",EDGE,"E61.MirrorCS");var subQ70=sQuery(id+"F8.wireOp",EDGE,"E36.MirrorCS");var subQ71=makeQuery(id+"F16.opExtrude","CAP_FACE",FACE,{"disambiguationData":[OSD([subQ70,subQ69,sQuery(id+"F8.wireOp",EDGE,"E105"),subQ68])],"isStart":true});var subQ72=sQuery(id+"F8.wireOp",EDGE,"E138");var subQ73=sQuery(id+"F8.wireOp",EDGE,"E60.MirrorCS");var subQ74=sQuery(id+"F8.wireOp",EDGE,"E35.MirrorCS");var subQ75=makeQuery(id+"F16.opExtrude","CAP_FACE",FACE,{"disambiguationData":[OSD([subQ74,subQ73,sQuery(id+"F8.wireOp",EDGE,"E103"),subQ72])],"isStart":true});var subQ76=sQuery(id+"F8.wireOp",EDGE,"E131");var subQ77=sQuery(id+"F8.wireOp",EDGE,"E53");var subQ78=sQuery(id+"F8.wireOp",EDGE,"E28");var subQ79=makeQuery(id+"F16.opExtrude","CAP_FACE",FACE,{"disambiguationData":[OSD([subQ78,subQ77,sQuery(id+"F8.wireOp",EDGE,"E89"),subQ76])],"isStart":true});var subQ80=makeQuery(id+"F17.opRevolve","CAP_FACE",FACE,{"disambiguationData":[OSD([subQ8,subQ38,subQ37,subQ36])],"isStart":true});var subQ81=sQuery(id+"F8.wireOp",EDGE,"E130");var subQ82=sQuery(id+"F8.wireOp",EDGE,"E52");var subQ83=sQuery(id+"F8.wireOp",EDGE,"E27");var subQ84=makeQuery(id+"F16.opExtrude","CAP_FACE",FACE,{"disambiguationData":[OSD([subQ83,subQ82,sQuery(id+"F8.wireOp",EDGE,"E87"),subQ81])],"isStart":true});var subQ85=sQuery(id+"F8.wireOp",EDGE,"E144");var subQ86=sQuery(id+"F8.wireOp",EDGE,"E143");var subQ87=sQuery(id+"F8.wireOp",EDGE,"E142");var subQ88=sQuery(id+"F8.wireOp",EDGE,"E137");var subQ89=sQuery(id+"F8.wireOp",EDGE,"E136");var subQ90=sQuery(id+"F8.wireOp",EDGE,"E135");var subQ91=sQuery(id+"F8.wireOp",EDGE,"E134");var subQ92=sQuery(id+"F8.wireOp",EDGE,"E133");var subQ93=sQuery(id+"F8.wireOp",EDGE,"E132");var subQ94=sQuery(id+"F8.wireOp",EDGE,"E124");var subQ95=sQuery(id+"F8.wireOp",EDGE,"E122");var subQ96=sQuery(id+"F8.wireOp",EDGE,"E119");var subQ97=sQuery(id+"F8.wireOp",EDGE,"E118");var subQ98=sQuery(id+"F8.wireOp",EDGE,"E116");var subQ99=sQuery(id+"F8.wireOp",EDGE,"E114");var subQ100=sQuery(id+"F8.wireOp",EDGE,"E112");var subQ101=sQuery(id+"F8.wireOp",EDGE,"E110");var subQ102=sQuery(id+"F8.wireOp",EDGE,"E108");var subQ103=sQuery(id+"F8.wireOp",EDGE,"E106");var subQ104=sQuery(id+"F8.wireOp",EDGE,"E104");var subQ105=sQuery(id+"F8.wireOp",EDGE,"E102");var subQ106=sQuery(id+"F8.wireOp",EDGE,"E100");var subQ107=sQuery(id+"F8.wireOp",EDGE,"E98");var subQ108=sQuery(id+"F8.wireOp",EDGE,"E96");var subQ109=sQuery(id+"F8.wireOp",EDGE,"E94");var subQ110=sQuery(id+"F8.wireOp",EDGE,"E92");var subQ111=sQuery(id+"F8.wireOp",EDGE,"E90");var subQ112=sQuery(id+"F8.wireOp",EDGE,"E88");var subQ113=sQuery(id+"F8.wireOp",EDGE,"E86");var subQ114=sQuery(id+"F8.wireOp",EDGE,"E84");var subQ115=sQuery(id+"F8.wireOp",EDGE,"E82");var subQ116=sQuery(id+"F8.wireOp",EDGE,"E80");var subQ117=sQuery(id+"F8.wireOp",EDGE,"E78");var subQ118=sQuery(id+"F8.wireOp",EDGE,"E76");var subQ119=sQuery(id+"F8.wireOp",EDGE,"E72.MirrorCS");var subQ120=sQuery(id+"F8.wireOp",EDGE,"E71.MirrorCS");var subQ121=sQuery(id+"F8.wireOp",EDGE,"E70.MirrorCS");var subQ122=sQuery(id+"F8.wireOp",EDGE,"E67.MirrorCS");var subQ123=sQuery(id+"F8.wireOp",EDGE,"E59.MirrorCS");var subQ124=sQuery(id+"F8.wireOp",EDGE,"E58.MirrorCS");var subQ125=sQuery(id+"F8.wireOp",EDGE,"E57");var subQ126=sQuery(id+"F8.wireOp",EDGE,"E56");var subQ127=sQuery(id+"F8.wireOp",EDGE,"E55");var subQ128=sQuery(id+"F8.wireOp",EDGE,"E54");var subQ129=sQuery(id+"F8.wireOp",EDGE,"E50");var subQ130=sQuery(id+"F8.wireOp",EDGE,"E49");var subQ131=sQuery(id+"F8.wireOp",EDGE,"E48.MirrorCS");var subQ132=sQuery(id+"F8.wireOp",EDGE,"E47.MirrorCS");var subQ133=sQuery(id+"F8.wireOp",EDGE,"E34.MirrorCS");var subQ134=sQuery(id+"F8.wireOp",EDGE,"E33");var subQ135=sQuery(id+"F8.wireOp",EDGE,"E32");var subQ136=sQuery(id+"F8.wireOp",EDGE,"E31");var subQ137=sQuery(id+"F8.wireOp",EDGE,"E30");var subQ138=sQuery(id+"F8.wireOp",EDGE,"E29");var subQ139=sQuery(id+"F8.wireOp",EDGE,"E1.0");var subQ140=makeQuery(id+"F15.opExtrude","CAP_FACE",FACE,{"disambiguationData":[OSD([subQ139,subQ83,subQ78,subQ138,subQ137,subQ136,subQ135,subQ134,subQ133,subQ74,subQ70,subQ66,subQ62,subQ58,subQ54,subQ50,subQ46,subQ42,subQ34,subQ29,subQ19,subQ132,subQ131,subQ130,subQ129,subQ57,subQ82,subQ77,subQ128,subQ127,subQ126,subQ125,subQ124,subQ123,subQ73,subQ69,subQ65,subQ53,subQ49,subQ45,subQ41,subQ122,subQ28,subQ18,subQ121,subQ120,subQ119,subQ61,subQ33,subQ118,subQ117,subQ116,subQ115,subQ114,subQ113,subQ112,subQ111,subQ110,subQ109,subQ108,subQ107,subQ106,subQ105,subQ104,subQ103,subQ102,subQ101,subQ100,subQ99,subQ98,subQ97,subQ96,subQ95,subQ94,subQ40,subQ44,subQ48,subQ52,subQ56,subQ81,subQ76,subQ93,subQ92,subQ91,subQ90,subQ89,subQ88,subQ72,subQ68,subQ64,subQ60,subQ87,subQ86,subQ85,subQ17,subQ27,subQ32])],"isStart":true});var subQ141=makeQuery(id+"F16.opExtrude","CAP_FACE",FACE,{"disambiguationData":[OSD([subQ129,subQ122,sQuery(id+"F8.wireOp",EDGE,"E123"),subQ94])],"isStart":true});var subQ142=makeQuery(id+"F16.opExtrude","CAP_FACE",FACE,{"disambiguationData":[OSD([subQ134,subQ124,sQuery(id+"F8.wireOp",EDGE,"E99"),subQ89])],"isStart":true});var subQ143=makeQuery(id+"F16.opExtrude","CAP_FACE",FACE,{"disambiguationData":[OSD([subQ138,subQ128,sQuery(id+"F8.wireOp",EDGE,"E91"),subQ93])],"isStart":true});var subQ144=makeQuery(id+"F16.opExtrude","CAP_FACE",FACE,{"disambiguationData":[OSD([subQ137,subQ127,sQuery(id+"F8.wireOp",EDGE,"E93"),subQ92])],"isStart":true});var subQ145=makeQuery(id+"F19.opExtrude","CAP_FACE",FACE,{"disambiguationData":[OSD([subQ25,subQ24,subQ15,subQ23,subQ22,subQ21])],"isStart":true});var subQ146=makeQuery(id+"F16.opExtrude","CAP_FACE",FACE,{"disambiguationData":[OSD([subQ136,subQ126,sQuery(id+"F8.wireOp",EDGE,"E95"),subQ91])],"isStart":true});var subQ147=makeQuery(id+"F15.opExtrude","CAP_FACE",FACE,{"disambiguationData":[OSD([subQ139,subQ83,subQ78,subQ138,subQ137,subQ136,subQ135,subQ134,subQ133,subQ74,subQ70,subQ66,subQ62,subQ58,subQ54,subQ50,subQ46,subQ42,subQ34,subQ29,subQ19,subQ132,subQ131,subQ130,subQ129,subQ57,subQ82,subQ77,subQ128,subQ127,subQ126,subQ125,subQ124,subQ123,subQ73,subQ69,subQ65,subQ53,subQ49,subQ45,subQ41,subQ122,subQ28,subQ18,subQ121,subQ120,subQ119,subQ61,subQ33,subQ118,subQ117,subQ116,subQ115,subQ114,subQ113,subQ112,subQ111,subQ110,subQ109,subQ108,subQ107,subQ106,subQ105,subQ104,subQ103,subQ102,subQ101,subQ100,subQ99,subQ98,subQ97,subQ96,subQ95,subQ94,subQ40,subQ44,subQ48,subQ52,subQ56,subQ81,subQ76,subQ93,subQ92,subQ91,subQ90,subQ89,subQ88,subQ72,subQ68,subQ64,subQ60,subQ87,subQ86,subQ85,subQ17,subQ27,subQ32])],"isStart":false});var subQ148=makeQuery(id+"F16.opExtrude","CAP_FACE",FACE,{"disambiguationData":[OSD([subQ135,subQ125,sQuery(id+"F8.wireOp",EDGE,"E97"),subQ90])],"isStart":true});var subQ149=makeQuery(id+"F19.opExtrude","SWEPT_FACE",FACE,{"disambiguationData":[OSD([subQ21])]});var subQ150=makeQuery(id+"F16.opExtrude","CAP_FACE",FACE,{"disambiguationData":[OSD([subQ133,subQ123,sQuery(id+"F8.wireOp",EDGE,"E101"),subQ88])],"isStart":true});var subQ151=makeQuery(id+"F16.opExtrude","CAP_FACE",FACE,{"disambiguationData":[OSD([subQ132,subQ121,sQuery(id+"F8.wireOp",EDGE,"E115"),subQ85])],"isStart":true});var subQ152=makeQuery(id+"F16.opExtrude","CAP_FACE",FACE,{"disambiguationData":[OSD([subQ131,subQ120,sQuery(id+"F8.wireOp",EDGE,"E113"),subQ86])],"isStart":true});var subQ153=makeQuery(id+"F16.opExtrude","CAP_FACE",FACE,{"disambiguationData":[OSD([subQ130,subQ119,sQuery(id+"F8.wireOp",EDGE,"E111"),subQ87])],"isStart":true});var subQ154=makeQuery(id+"F18.opRevolve","SWEPT_FACE",FACE,{"disambiguationData":[OSD([subQ36])]});var subQ155=makeQuery(id+"F19.opExtrude","SWEPT_FACE",FACE,{"disambiguationData":[OSD([subQ24])]});var subQ156=makeQuery(id+"F19.opExtrude","SWEPT_FACE",FACE,{"disambiguationData":[OSD([subQ22])]});Q7=makeQuery(id+"F38.opFillet","BLEND_EDGE",EDGE,{"blendedFrom":[makeQuery(id+"F21.boolean.opBoolean","INTERSECT",EDGE,{"derivedFrom":[makeQuery(id+"F20.boolean.opBoolean","SPLIT",FACE,{"disambiguationData":[TD([subQ31])],"derivedFrom":makeQuery(id+"F19.boolean.opBoolean","SPLIT",FACE,{"disambiguationData":[TD([makeQuery(id+"F15.opExtrude","SWEPT_FACE",FACE,{"disambiguationData":[OSD([subQ139])]}),subQ140,subQ147,subQ84,subQ79,subQ143,subQ144,subQ146,subQ148,subQ142,subQ150,subQ75,subQ71,subQ67,subQ63,subQ59,subQ55,subQ51,subQ47,subQ43,subQ35,subQ30,subQ20,subQ151,subQ152,subQ153,subQ141,subQ80,subQ39,subQ31,subQ154,subQ145,subQ26,subQ155,subQ16,subQ156,subQ149])],"derivedFrom":makeQuery(id+"F18.boolean.opBoolean","MERGE",FACE,{"derivedFrom":[subQ10,subQ9]})})}),subQ12]}),makeQuery(id+"F24.boolean.opBoolean","SPLIT",FACE,{"disambiguationData":[TD([subQ11])],"derivedFrom":makeQuery(id+"F23.boolean.opBoolean","MERGE",FACE,{"derivedFrom":[subQ16,subQ14,makeQuery(id+"F23.opExtrude","CAP_FACE",FACE,{"disambiguationData":[OSD([sQuery(id+"F13.wireOp",EDGE,"E297.MirrorCS"),sQuery(id+"F13.wireOp",EDGE,"E307"),sQuery(id+"F13.wireOp",EDGE,"E308"),subQ13,sQuery(id+"F13.wireOp",EDGE,"E310.0"),sQuery(id+"F13.wireOp",EDGE,"E310.1"),sQuery(id+"F13.wireOp",EDGE,"E310.2")])],"isStart":false})]})})],"blendedInto":[makeQuery(id+"F24.boolean.opBoolean","SPLIT",FACE,{"disambiguationData":[TD([subQ11])],"derivedFrom":makeQuery(id+"F23.boolean.opBoolean","MERGE",FACE,{"derivedFrom":[subQ16,subQ14,makeQuery(id+"F23.opExtrude","CAP_FACE",FACE,{"disambiguationData":[OSD([sQuery(id+"F13.wireOp",EDGE,"E297.MirrorCS"),sQuery(id+"F13.wireOp",EDGE,"E307"),sQuery(id+"F13.wireOp",EDGE,"E308"),subQ13,sQuery(id+"F13.wireOp",EDGE,"E310.0"),sQuery(id+"F13.wireOp",EDGE,"E310.1"),sQuery(id+"F13.wireOp",EDGE,"E310.2")])],"isStart":false})]})})]});}
            var Q8;
            {var subQ0=sQuery(id+"F12.wireOp",EDGE,"E290");var subQ1=sQuery(id+"F12.wireOp",EDGE,"E289");var subQ2=sQuery(id+"F12.wireOp",EDGE,"E288");var subQ3=sQuery(id+"F12.wireOp",EDGE,"E287");var subQ4=sQuery(id+"F12.wireOp",EDGE,"E286");var subQ5=sQuery(id+"F12.wireOp",EDGE,"E285");var subQ6=makeQuery(id+"F19.opExtrude","CAP_FACE",FACE,{"disambiguationData":[OSD([subQ5,subQ4,subQ3,subQ2,subQ1,subQ0])],"isStart":false});var subQ7=sQuery(id+"F9.wireOp",EDGE,"E150");var subQ8=makeQuery(id+"F18.opRevolve","SWEPT_FACE",FACE,{"disambiguationData":[OSD([subQ7])]});var subQ9=makeQuery(id+"F19.opExtrude","SWEPT_FACE",FACE,{"disambiguationData":[OSD([subQ4])]});var subQ10=sQuery(id+"F13.wireOp",EDGE,"E307");var subQ11=makeQuery(id+"F19.opExtrude","CAP_FACE",FACE,{"disambiguationData":[OSD([subQ5,subQ4,subQ3,subQ2,subQ1,subQ0])],"isStart":true});var subQ12=makeQuery(id+"F17.opRevolve","SWEPT_FACE",FACE,{"disambiguationData":[OSD([subQ7])]});var subQ13=makeQuery(id+"F21.opExtrude","SWEPT_FACE",FACE,{"disambiguationData":[OSD([sQuery(id+"F13.wireOp",EDGE,"E295.MirrorCS")])]});var subQ14=sQuery(id+"F11.wireOp",EDGE,"E261");var subQ15=makeQuery(id+"F20.opExtrude","SWEPT_FACE",FACE,{"disambiguationData":[OSD([subQ14])]});var subQ16=makeQuery(id+"F19.opExtrude","SWEPT_FACE",FACE,{"disambiguationData":[OSD([subQ3])]});var subQ17=sQuery(id+"F8.wireOp",EDGE,"E145");var subQ18=sQuery(id+"F8.wireOp",EDGE,"E69.MirrorCS");var subQ19=sQuery(id+"F8.wireOp",EDGE,"E46.MirrorCS");var subQ20=makeQuery(id+"F16.opExtrude","CAP_FACE",FACE,{"disambiguationData":[OSD([subQ19,subQ18,sQuery(id+"F8.wireOp",EDGE,"E117"),subQ17])],"isStart":true});var subQ21=sQuery(id+"F8.wireOp",EDGE,"E146");var subQ22=sQuery(id+"F8.wireOp",EDGE,"E68.MirrorCS");var subQ23=sQuery(id+"F8.wireOp",EDGE,"E45.MirrorCS");var subQ24=makeQuery(id+"F16.opExtrude","CAP_FACE",FACE,{"disambiguationData":[OSD([subQ23,subQ22,sQuery(id+"F8.wireOp",EDGE,"E120"),subQ21])],"isStart":true});var subQ25=makeQuery(id+"F18.opRevolve","SWEPT_FACE",FACE,{"disambiguationData":[OSD([sQuery(id+"F9.wireOp",EDGE,"E157")])]});var subQ26=sQuery(id+"F8.wireOp",EDGE,"E147");var subQ27=sQuery(id+"F8.wireOp",EDGE,"E74");var subQ28=sQuery(id+"F8.wireOp",EDGE,"E44.MirrorCS");var subQ29=makeQuery(id+"F16.opExtrude","CAP_FACE",FACE,{"disambiguationData":[OSD([subQ28,subQ27,sQuery(id+"F8.wireOp",EDGE,"E121"),subQ26])],"isStart":true});var subQ30=sQuery(id+"F9.wireOp",EDGE,"E164");var subQ31=sQuery(id+"F9.wireOp",EDGE,"E152");var subQ32=sQuery(id+"F9.wireOp",EDGE,"E151");var subQ33=makeQuery(id+"F17.opRevolve","CAP_FACE",FACE,{"disambiguationData":[OSD([subQ7,subQ32,subQ31,subQ30])],"isStart":false});var subQ34=sQuery(id+"F8.wireOp",EDGE,"E125");var subQ35=sQuery(id+"F8.wireOp",EDGE,"E66.MirrorCS");var subQ36=sQuery(id+"F8.wireOp",EDGE,"E43.MirrorCS");var subQ37=makeQuery(id+"F16.opExtrude","CAP_FACE",FACE,{"disambiguationData":[OSD([subQ36,subQ35,sQuery(id+"F8.wireOp",EDGE,"E77"),subQ34])],"isStart":true});var subQ38=sQuery(id+"F8.wireOp",EDGE,"E126");var subQ39=sQuery(id+"F8.wireOp",EDGE,"E65.MirrorCS");var subQ40=sQuery(id+"F8.wireOp",EDGE,"E42.MirrorCS");var subQ41=makeQuery(id+"F16.opExtrude","CAP_FACE",FACE,{"disambiguationData":[OSD([subQ40,subQ39,sQuery(id+"F8.wireOp",EDGE,"E79"),subQ38])],"isStart":true});var subQ42=sQuery(id+"F8.wireOp",EDGE,"E127");var subQ43=sQuery(id+"F8.wireOp",EDGE,"E64.MirrorCS");var subQ44=sQuery(id+"F8.wireOp",EDGE,"E41.MirrorCS");var subQ45=makeQuery(id+"F16.opExtrude","CAP_FACE",FACE,{"disambiguationData":[OSD([subQ44,subQ43,sQuery(id+"F8.wireOp",EDGE,"E81"),subQ42])],"isStart":true});var subQ46=sQuery(id+"F8.wireOp",EDGE,"E128");var subQ47=sQuery(id+"F8.wireOp",EDGE,"E63.MirrorCS");var subQ48=sQuery(id+"F8.wireOp",EDGE,"E40.MirrorCS");var subQ49=makeQuery(id+"F16.opExtrude","CAP_FACE",FACE,{"disambiguationData":[OSD([subQ48,subQ47,sQuery(id+"F8.wireOp",EDGE,"E83"),subQ46])],"isStart":true});var subQ50=sQuery(id+"F8.wireOp",EDGE,"E129");var subQ51=sQuery(id+"F8.wireOp",EDGE,"E51");var subQ52=sQuery(id+"F8.wireOp",EDGE,"E39.MirrorCS");var subQ53=makeQuery(id+"F16.opExtrude","CAP_FACE",FACE,{"disambiguationData":[OSD([subQ52,subQ51,sQuery(id+"F8.wireOp",EDGE,"E85"),subQ50])],"isStart":true});var subQ54=sQuery(id+"F8.wireOp",EDGE,"E141");var subQ55=sQuery(id+"F8.wireOp",EDGE,"E73");var subQ56=sQuery(id+"F8.wireOp",EDGE,"E38.MirrorCS");var subQ57=makeQuery(id+"F16.opExtrude","CAP_FACE",FACE,{"disambiguationData":[OSD([subQ56,subQ55,sQuery(id+"F8.wireOp",EDGE,"E109"),subQ54])],"isStart":true});var subQ58=sQuery(id+"F8.wireOp",EDGE,"E140");var subQ59=sQuery(id+"F8.wireOp",EDGE,"E62.MirrorCS");var subQ60=sQuery(id+"F8.wireOp",EDGE,"E37.MirrorCS");var subQ61=makeQuery(id+"F16.opExtrude","CAP_FACE",FACE,{"disambiguationData":[OSD([subQ60,subQ59,sQuery(id+"F8.wireOp",EDGE,"E107"),subQ58])],"isStart":true});var subQ62=sQuery(id+"F8.wireOp",EDGE,"E139");var subQ63=sQuery(id+"F8.wireOp",EDGE,"E61.MirrorCS");var subQ64=sQuery(id+"F8.wireOp",EDGE,"E36.MirrorCS");var subQ65=makeQuery(id+"F16.opExtrude","CAP_FACE",FACE,{"disambiguationData":[OSD([subQ64,subQ63,sQuery(id+"F8.wireOp",EDGE,"E105"),subQ62])],"isStart":true});var subQ66=sQuery(id+"F8.wireOp",EDGE,"E138");var subQ67=sQuery(id+"F8.wireOp",EDGE,"E60.MirrorCS");var subQ68=sQuery(id+"F8.wireOp",EDGE,"E35.MirrorCS");var subQ69=makeQuery(id+"F16.opExtrude","CAP_FACE",FACE,{"disambiguationData":[OSD([subQ68,subQ67,sQuery(id+"F8.wireOp",EDGE,"E103"),subQ66])],"isStart":true});var subQ70=sQuery(id+"F8.wireOp",EDGE,"E131");var subQ71=sQuery(id+"F8.wireOp",EDGE,"E53");var subQ72=sQuery(id+"F8.wireOp",EDGE,"E28");var subQ73=makeQuery(id+"F16.opExtrude","CAP_FACE",FACE,{"disambiguationData":[OSD([subQ72,subQ71,sQuery(id+"F8.wireOp",EDGE,"E89"),subQ70])],"isStart":true});var subQ74=makeQuery(id+"F17.opRevolve","CAP_FACE",FACE,{"disambiguationData":[OSD([subQ7,subQ32,subQ31,subQ30])],"isStart":true});var subQ75=sQuery(id+"F8.wireOp",EDGE,"E130");var subQ76=sQuery(id+"F8.wireOp",EDGE,"E52");var subQ77=sQuery(id+"F8.wireOp",EDGE,"E27");var subQ78=makeQuery(id+"F16.opExtrude","CAP_FACE",FACE,{"disambiguationData":[OSD([subQ77,subQ76,sQuery(id+"F8.wireOp",EDGE,"E87"),subQ75])],"isStart":true});var subQ79=sQuery(id+"F8.wireOp",EDGE,"E144");var subQ80=sQuery(id+"F8.wireOp",EDGE,"E143");var subQ81=sQuery(id+"F8.wireOp",EDGE,"E142");var subQ82=sQuery(id+"F8.wireOp",EDGE,"E137");var subQ83=sQuery(id+"F8.wireOp",EDGE,"E136");var subQ84=sQuery(id+"F8.wireOp",EDGE,"E135");var subQ85=sQuery(id+"F8.wireOp",EDGE,"E134");var subQ86=sQuery(id+"F8.wireOp",EDGE,"E133");var subQ87=sQuery(id+"F8.wireOp",EDGE,"E132");var subQ88=sQuery(id+"F8.wireOp",EDGE,"E124");var subQ89=sQuery(id+"F8.wireOp",EDGE,"E122");var subQ90=sQuery(id+"F8.wireOp",EDGE,"E119");var subQ91=sQuery(id+"F8.wireOp",EDGE,"E118");var subQ92=sQuery(id+"F8.wireOp",EDGE,"E116");var subQ93=sQuery(id+"F8.wireOp",EDGE,"E114");var subQ94=sQuery(id+"F8.wireOp",EDGE,"E112");var subQ95=sQuery(id+"F8.wireOp",EDGE,"E110");var subQ96=sQuery(id+"F8.wireOp",EDGE,"E108");var subQ97=sQuery(id+"F8.wireOp",EDGE,"E106");var subQ98=sQuery(id+"F8.wireOp",EDGE,"E104");var subQ99=sQuery(id+"F8.wireOp",EDGE,"E102");var subQ100=sQuery(id+"F8.wireOp",EDGE,"E100");var subQ101=sQuery(id+"F8.wireOp",EDGE,"E98");var subQ102=sQuery(id+"F8.wireOp",EDGE,"E96");var subQ103=sQuery(id+"F8.wireOp",EDGE,"E94");var subQ104=sQuery(id+"F8.wireOp",EDGE,"E92");var subQ105=sQuery(id+"F8.wireOp",EDGE,"E90");var subQ106=sQuery(id+"F8.wireOp",EDGE,"E88");var subQ107=sQuery(id+"F8.wireOp",EDGE,"E86");var subQ108=sQuery(id+"F8.wireOp",EDGE,"E84");var subQ109=sQuery(id+"F8.wireOp",EDGE,"E82");var subQ110=sQuery(id+"F8.wireOp",EDGE,"E80");var subQ111=sQuery(id+"F8.wireOp",EDGE,"E78");var subQ112=sQuery(id+"F8.wireOp",EDGE,"E76");var subQ113=sQuery(id+"F8.wireOp",EDGE,"E72.MirrorCS");var subQ114=sQuery(id+"F8.wireOp",EDGE,"E71.MirrorCS");var subQ115=sQuery(id+"F8.wireOp",EDGE,"E70.MirrorCS");var subQ116=sQuery(id+"F8.wireOp",EDGE,"E67.MirrorCS");var subQ117=sQuery(id+"F8.wireOp",EDGE,"E59.MirrorCS");var subQ118=sQuery(id+"F8.wireOp",EDGE,"E58.MirrorCS");var subQ119=sQuery(id+"F8.wireOp",EDGE,"E57");var subQ120=sQuery(id+"F8.wireOp",EDGE,"E56");var subQ121=sQuery(id+"F8.wireOp",EDGE,"E55");var subQ122=sQuery(id+"F8.wireOp",EDGE,"E54");var subQ123=sQuery(id+"F8.wireOp",EDGE,"E50");var subQ124=sQuery(id+"F8.wireOp",EDGE,"E49");var subQ125=sQuery(id+"F8.wireOp",EDGE,"E48.MirrorCS");var subQ126=sQuery(id+"F8.wireOp",EDGE,"E47.MirrorCS");var subQ127=sQuery(id+"F8.wireOp",EDGE,"E34.MirrorCS");var subQ128=sQuery(id+"F8.wireOp",EDGE,"E33");var subQ129=sQuery(id+"F8.wireOp",EDGE,"E32");var subQ130=sQuery(id+"F8.wireOp",EDGE,"E31");var subQ131=sQuery(id+"F8.wireOp",EDGE,"E30");var subQ132=sQuery(id+"F8.wireOp",EDGE,"E29");var subQ133=sQuery(id+"F8.wireOp",EDGE,"E1.0");var subQ134=makeQuery(id+"F15.opExtrude","CAP_FACE",FACE,{"disambiguationData":[OSD([subQ133,subQ77,subQ72,subQ132,subQ131,subQ130,subQ129,subQ128,subQ127,subQ68,subQ64,subQ60,subQ56,subQ52,subQ48,subQ44,subQ40,subQ36,subQ28,subQ23,subQ19,subQ126,subQ125,subQ124,subQ123,subQ51,subQ76,subQ71,subQ122,subQ121,subQ120,subQ119,subQ118,subQ117,subQ67,subQ63,subQ59,subQ47,subQ43,subQ39,subQ35,subQ116,subQ22,subQ18,subQ115,subQ114,subQ113,subQ55,subQ27,subQ112,subQ111,subQ110,subQ109,subQ108,subQ107,subQ106,subQ105,subQ104,subQ103,subQ102,subQ101,subQ100,subQ99,subQ98,subQ97,subQ96,subQ95,subQ94,subQ93,subQ92,subQ91,subQ90,subQ89,subQ88,subQ34,subQ38,subQ42,subQ46,subQ50,subQ75,subQ70,subQ87,subQ86,subQ85,subQ84,subQ83,subQ82,subQ66,subQ62,subQ58,subQ54,subQ81,subQ80,subQ79,subQ17,subQ21,subQ26])],"isStart":true});var subQ135=makeQuery(id+"F16.opExtrude","CAP_FACE",FACE,{"disambiguationData":[OSD([subQ123,subQ116,sQuery(id+"F8.wireOp",EDGE,"E123"),subQ88])],"isStart":true});var subQ136=makeQuery(id+"F16.opExtrude","CAP_FACE",FACE,{"disambiguationData":[OSD([subQ128,subQ118,sQuery(id+"F8.wireOp",EDGE,"E99"),subQ83])],"isStart":true});var subQ138=makeQuery(id+"F16.opExtrude","CAP_FACE",FACE,{"disambiguationData":[OSD([subQ132,subQ122,sQuery(id+"F8.wireOp",EDGE,"E91"),subQ87])],"isStart":true});var subQ139=makeQuery(id+"F16.opExtrude","CAP_FACE",FACE,{"disambiguationData":[OSD([subQ131,subQ121,sQuery(id+"F8.wireOp",EDGE,"E93"),subQ86])],"isStart":true});var subQ140=makeQuery(id+"F16.opExtrude","CAP_FACE",FACE,{"disambiguationData":[OSD([subQ130,subQ120,sQuery(id+"F8.wireOp",EDGE,"E95"),subQ85])],"isStart":true});var subQ145=makeQuery(id+"F15.opExtrude","CAP_FACE",FACE,{"disambiguationData":[OSD([subQ133,subQ77,subQ72,subQ132,subQ131,subQ130,subQ129,subQ128,subQ127,subQ68,subQ64,subQ60,subQ56,subQ52,subQ48,subQ44,subQ40,subQ36,subQ28,subQ23,subQ19,subQ126,subQ125,subQ124,subQ123,subQ51,subQ76,subQ71,subQ122,subQ121,subQ120,subQ119,subQ118,subQ117,subQ67,subQ63,subQ59,subQ47,subQ43,subQ39,subQ35,subQ116,subQ22,subQ18,subQ115,subQ114,subQ113,subQ55,subQ27,subQ112,subQ111,subQ110,subQ109,subQ108,subQ107,subQ106,subQ105,subQ104,subQ103,subQ102,subQ101,subQ100,subQ99,subQ98,subQ97,subQ96,subQ95,subQ94,subQ93,subQ92,subQ91,subQ90,subQ89,subQ88,subQ34,subQ38,subQ42,subQ46,subQ50,subQ75,subQ70,subQ87,subQ86,subQ85,subQ84,subQ83,subQ82,subQ66,subQ62,subQ58,subQ54,subQ81,subQ80,subQ79,subQ17,subQ21,subQ26])],"isStart":false});var subQ146=makeQuery(id+"F16.opExtrude","CAP_FACE",FACE,{"disambiguationData":[OSD([subQ129,subQ119,sQuery(id+"F8.wireOp",EDGE,"E97"),subQ84])],"isStart":true});var subQ147=makeQuery(id+"F19.opExtrude","SWEPT_FACE",FACE,{"disambiguationData":[OSD([subQ0])]});var subQ148=makeQuery(id+"F16.opExtrude","CAP_FACE",FACE,{"disambiguationData":[OSD([subQ127,subQ117,sQuery(id+"F8.wireOp",EDGE,"E101"),subQ82])],"isStart":true});var subQ149=makeQuery(id+"F16.opExtrude","CAP_FACE",FACE,{"disambiguationData":[OSD([subQ126,subQ115,sQuery(id+"F8.wireOp",EDGE,"E115"),subQ79])],"isStart":true});var subQ150=makeQuery(id+"F16.opExtrude","CAP_FACE",FACE,{"disambiguationData":[OSD([subQ125,subQ114,sQuery(id+"F8.wireOp",EDGE,"E113"),subQ80])],"isStart":true});var subQ151=makeQuery(id+"F16.opExtrude","CAP_FACE",FACE,{"disambiguationData":[OSD([subQ124,subQ113,sQuery(id+"F8.wireOp",EDGE,"E111"),subQ81])],"isStart":true});var subQ152=makeQuery(id+"F18.opRevolve","SWEPT_FACE",FACE,{"disambiguationData":[OSD([subQ30])]});var subQ153=makeQuery(id+"F19.opExtrude","SWEPT_FACE",FACE,{"disambiguationData":[OSD([subQ1])]});Q8=makeQuery(id+"F38.opFillet","BLEND_EDGE",EDGE,{"blendedFrom":[makeQuery(id+"F21.boolean.opBoolean","INTERSECT",EDGE,{"derivedFrom":[makeQuery(id+"F20.boolean.opBoolean","SPLIT",FACE,{"disambiguationData":[TD([subQ25])],"derivedFrom":makeQuery(id+"F19.boolean.opBoolean","SPLIT",FACE,{"disambiguationData":[TD([makeQuery(id+"F15.opExtrude","SWEPT_FACE",FACE,{"disambiguationData":[OSD([subQ133])]}),subQ134,subQ145,subQ78,subQ73,subQ138,subQ139,subQ140,subQ146,subQ136,subQ148,subQ69,subQ65,subQ61,subQ57,subQ53,subQ49,subQ45,subQ41,subQ37,subQ29,subQ24,subQ20,subQ149,subQ150,subQ151,subQ135,subQ74,subQ33,subQ25,subQ152,subQ11,subQ6,subQ9,subQ16,subQ153,subQ147])],"derivedFrom":makeQuery(id+"F18.boolean.opBoolean","MERGE",FACE,{"derivedFrom":[subQ12,subQ8]})})}),subQ13]}),makeQuery(id+"F24.boolean.opBoolean","SPLIT",FACE,{"disambiguationData":[TD([subQ9])],"derivedFrom":makeQuery(id+"F23.boolean.opBoolean","MERGE",FACE,{"derivedFrom":[subQ16,subQ15,makeQuery(id+"F23.opExtrude","CAP_FACE",FACE,{"disambiguationData":[OSD([sQuery(id+"F13.wireOp",EDGE,"E297.MirrorCS"),subQ10,sQuery(id+"F13.wireOp",EDGE,"E308"),sQuery(id+"F13.wireOp",EDGE,"E309"),sQuery(id+"F13.wireOp",EDGE,"E310.0"),sQuery(id+"F13.wireOp",EDGE,"E310.1"),sQuery(id+"F13.wireOp",EDGE,"E310.2")])],"isStart":false})]})})],"blendedInto":[makeQuery(id+"F24.boolean.opBoolean","SPLIT",FACE,{"disambiguationData":[TD([subQ9])],"derivedFrom":makeQuery(id+"F23.boolean.opBoolean","MERGE",FACE,{"derivedFrom":[subQ16,subQ15,makeQuery(id+"F23.opExtrude","CAP_FACE",FACE,{"disambiguationData":[OSD([sQuery(id+"F13.wireOp",EDGE,"E297.MirrorCS"),subQ10,sQuery(id+"F13.wireOp",EDGE,"E308"),sQuery(id+"F13.wireOp",EDGE,"E309"),sQuery(id+"F13.wireOp",EDGE,"E310.0"),sQuery(id+"F13.wireOp",EDGE,"E310.1"),sQuery(id+"F13.wireOp",EDGE,"E310.2")])],"isStart":false})]})})]});}
            var Q9;
            Q9=makeQuery(id+"F25.opExtrude","CAP_EDGE",EDGE,{"disambiguationData":[OSD([sQuery(id+"F10.wireOp",EDGE,"E233")])],"isStart":true});
            var Q10;
            Q10=makeQuery(id+"F25.opExtrude","CAP_EDGE",EDGE,{"disambiguationData":[OSD([sQuery(id+"F10.wireOp",EDGE,"E234")])],"isStart":true});
            var Q11;
            Q11=makeQuery(id+"F25.opExtrude","CAP_EDGE",EDGE,{"disambiguationData":[OSD([sQuery(id+"F10.wireOp",EDGE,"oL6OTD61-6akg-XuXO-bSg7-LTXE6IEmyDXN")])],"isStart":true});
            var Q12;
            Q12=makeQuery(id+"F37.opExtrude","SWEPT_EDGE",EDGE,{"disambiguationData":[OSD([sQuery(id+"F31.wireOp",EDGE,"E362.0"),sQuery(id+"F31.wireOp",EDGE,"E364")])]});
            var Q13;
            Q13=makeQuery(id+"F37.opExtrude","SWEPT_EDGE",EDGE,{"disambiguationData":[OSD([sQuery(id+"F31.wireOp",EDGE,"E362.0"),sQuery(id+"F31.wireOp",EDGE,"E363")])]});
            var Q14;
            Q14=makeQuery(id+"F37.opExtrude","SWEPT_EDGE",EDGE,{"disambiguationData":[OSD([sQuery(id+"F31.wireOp",EDGE,"E360"),sQuery(id+"F31.wireOp",EDGE,"E364")])]});
            var Q15;
            Q15=makeQuery(id+"F37.opExtrude","SWEPT_EDGE",EDGE,{"disambiguationData":[OSD([sQuery(id+"F31.wireOp",EDGE,"E360"),sQuery(id+"F31.wireOp",EDGE,"E363")])]});
            fillet(context, id + "F39", {"entities" : qUnion([Q0, Q1, Q2, Q3, Q4, Q5, Q6, Q7, Q8, Q9, Q10, Q11, Q12, Q13, Q14, Q15]), "radius" : 2.6 * mm, "tangentPropagation" : true, "allowEdgeOverflow" : false});
        }
        {
            var Q0;
            Q0=makeQuery(id+"F16.opExtrude","CAP_EDGE",EDGE,{"disambiguationData":[OSD([sQuery(id+"F8.wireOp",EDGE,"E77")])],"isStart":false});
            var Q1;
            Q1=makeQuery(id+"F16.opExtrude","CAP_EDGE",EDGE,{"disambiguationData":[OSD([sQuery(id+"F8.wireOp",EDGE,"E79")])],"isStart":false});
            var Q2;
            Q2=makeQuery(id+"F16.opExtrude","CAP_EDGE",EDGE,{"disambiguationData":[OSD([sQuery(id+"F8.wireOp",EDGE,"E81")])],"isStart":false});
            var Q3;
            Q3=makeQuery(id+"F16.opExtrude","CAP_EDGE",EDGE,{"disambiguationData":[OSD([sQuery(id+"F8.wireOp",EDGE,"E83")])],"isStart":false});
            var Q4;
            Q4=makeQuery(id+"F16.opExtrude","CAP_EDGE",EDGE,{"disambiguationData":[OSD([sQuery(id+"F8.wireOp",EDGE,"E85")])],"isStart":false});
            var Q5;
            Q5=makeQuery(id+"F16.opExtrude","CAP_EDGE",EDGE,{"disambiguationData":[OSD([sQuery(id+"F8.wireOp",EDGE,"E87")])],"isStart":false});
            var Q6;
            Q6=makeQuery(id+"F16.opExtrude","CAP_EDGE",EDGE,{"disambiguationData":[OSD([sQuery(id+"F8.wireOp",EDGE,"E89")])],"isStart":false});
            var Q7;
            Q7=makeQuery(id+"F16.opExtrude","CAP_EDGE",EDGE,{"disambiguationData":[OSD([sQuery(id+"F8.wireOp",EDGE,"E91")])],"isStart":false});
            var Q8;
            Q8=makeQuery(id+"F16.opExtrude","CAP_EDGE",EDGE,{"disambiguationData":[OSD([sQuery(id+"F8.wireOp",EDGE,"E93")])],"isStart":false});
            var Q9;
            Q9=makeQuery(id+"F16.opExtrude","CAP_EDGE",EDGE,{"disambiguationData":[OSD([sQuery(id+"F8.wireOp",EDGE,"E95")])],"isStart":false});
            var Q10;
            Q10=makeQuery(id+"F16.opExtrude","CAP_EDGE",EDGE,{"disambiguationData":[OSD([sQuery(id+"F8.wireOp",EDGE,"E123")])],"isStart":false});
            var Q11;
            Q11=makeQuery(id+"F16.opExtrude","CAP_EDGE",EDGE,{"disambiguationData":[OSD([sQuery(id+"F8.wireOp",EDGE,"E121")])],"isStart":false});
            var Q12;
            Q12=makeQuery(id+"F16.opExtrude","CAP_EDGE",EDGE,{"disambiguationData":[OSD([sQuery(id+"F8.wireOp",EDGE,"E120")])],"isStart":false});
            var Q13;
            Q13=makeQuery(id+"F16.opExtrude","CAP_EDGE",EDGE,{"disambiguationData":[OSD([sQuery(id+"F8.wireOp",EDGE,"E117")])],"isStart":false});
            var Q14;
            Q14=makeQuery(id+"F16.opExtrude","CAP_EDGE",EDGE,{"disambiguationData":[OSD([sQuery(id+"F8.wireOp",EDGE,"E115")])],"isStart":false});
            var Q15;
            Q15=makeQuery(id+"F16.opExtrude","CAP_EDGE",EDGE,{"disambiguationData":[OSD([sQuery(id+"F8.wireOp",EDGE,"E113")])],"isStart":false});
            var Q16;
            Q16=makeQuery(id+"F16.opExtrude","CAP_EDGE",EDGE,{"disambiguationData":[OSD([sQuery(id+"F8.wireOp",EDGE,"E111")])],"isStart":false});
            var Q17;
            Q17=makeQuery(id+"F16.opExtrude","CAP_EDGE",EDGE,{"disambiguationData":[OSD([sQuery(id+"F8.wireOp",EDGE,"E109")])],"isStart":false});
            var Q18;
            Q18=makeQuery(id+"F16.opExtrude","CAP_EDGE",EDGE,{"disambiguationData":[OSD([sQuery(id+"F8.wireOp",EDGE,"E107")])],"isStart":false});
            var Q19;
            Q19=makeQuery(id+"F16.opExtrude","CAP_EDGE",EDGE,{"disambiguationData":[OSD([sQuery(id+"F8.wireOp",EDGE,"E105")])],"isStart":false});
            var Q20;
            Q20=makeQuery(id+"F16.opExtrude","CAP_EDGE",EDGE,{"disambiguationData":[OSD([sQuery(id+"F8.wireOp",EDGE,"E103")])],"isStart":false});
            var Q21;
            Q21=makeQuery(id+"F16.opExtrude","CAP_EDGE",EDGE,{"disambiguationData":[OSD([sQuery(id+"F8.wireOp",EDGE,"E101")])],"isStart":false});
            var Q22;
            Q22=makeQuery(id+"F16.opExtrude","CAP_EDGE",EDGE,{"disambiguationData":[OSD([sQuery(id+"F8.wireOp",EDGE,"E99")])],"isStart":false});
            var Q23;
            Q23=makeQuery(id+"F16.opExtrude","CAP_EDGE",EDGE,{"disambiguationData":[OSD([sQuery(id+"F8.wireOp",EDGE,"E97")])],"isStart":false});
            fillet(context, id + "F40", {"entities" : qUnion([Q0, Q1, Q2, Q3, Q4, Q5, Q6, Q7, Q8, Q9, Q10, Q11, Q12, Q13, Q14, Q15, Q16, Q17, Q18, Q19, Q20, Q21, Q22, Q23]), "radius" : 3 * mm, "tangentPropagation" : true, "allowEdgeOverflow" : false});
        }
    });
